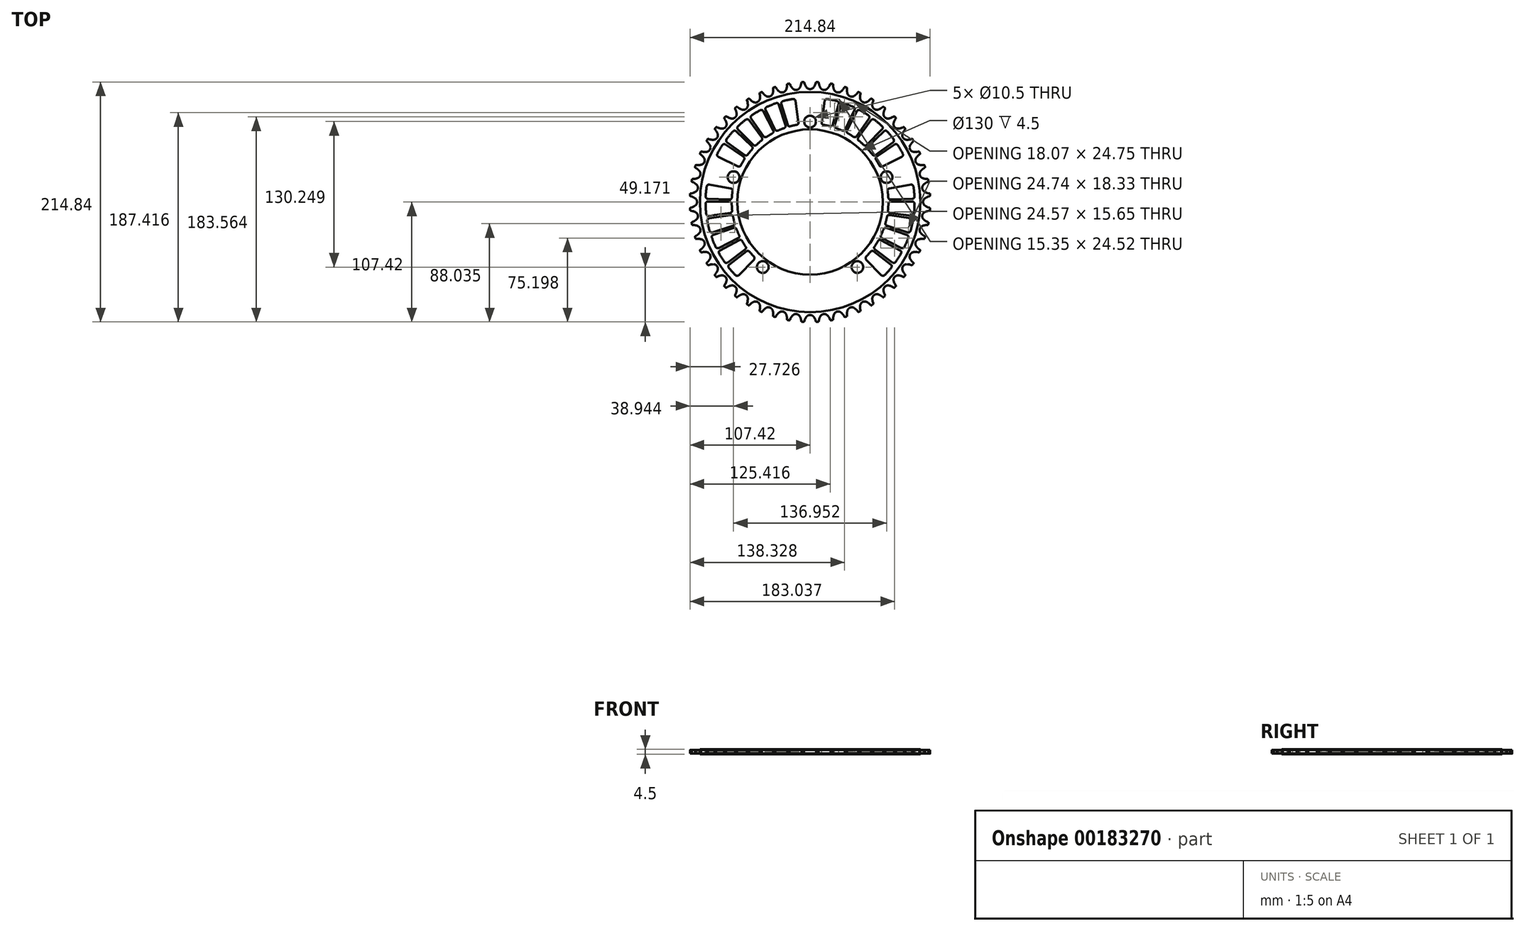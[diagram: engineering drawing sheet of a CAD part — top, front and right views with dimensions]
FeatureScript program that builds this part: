
annotation { "Feature Type Name" : "Feature", "Feature Type Description" : "" }
export const myFeature = defineFeature(function(context is Context, id is Id, definition is map)
    precondition{}
    {
        {
            var Q0;
            Q0=qCreatedBy(makeId("Top.planeOp"),FACE);
            var sketch = newSketch(context, id + "F0", { "sketchPlane" : qUnion([Q0])});
            skArc(sketch, "E0", {"start": v(-3.24, 102.74) * mm, "mid": v(-1.82, 101.53) * mm, "end": v(0, 101.1) * mm});
            skArc(sketch, "E1", {"start": v(-4.68, 105.43) * mm, "mid": v(-4.06, 104.03) * mm, "end": v(-3.24, 102.74) * mm});
            skLineSegment(sketch, "E2", {"start": v(-4.68, 105.43) * mm, "end": v(-5.06, 106.54) * mm});
            skArc(sketch, "E3.trimOffspring", {"start": v(-5.06, 106.54) * mm, "mid": v(-5.7, 107.84) * mm, "end": v(-6.6, 108.97) * mm});
            skArc(sketch, "E4.MirrorCS", {"start": v(3.24, 102.74) * mm, "mid": v(1.82, 101.53) * mm, "end": v(0, 101.1) * mm});
            skArc(sketch, "E5.MirrorCS", {"start": v(4.68, 105.43) * mm, "mid": v(4.06, 104.03) * mm, "end": v(3.24, 102.74) * mm});
            skLineSegment(sketch, "E6.MirrorCS", {"start": v(4.68, 105.43) * mm, "end": v(5.06, 106.54) * mm});
            skArc(sketch, "E7.MirrorCS", {"start": v(5.06, 106.54) * mm, "mid": v(5.7, 107.84) * mm, "end": v(6.6, 108.97) * mm});
            skArc(sketch, "E8.1.0", {"start": v(-17.35, 104.1) * mm, "mid": v(-16.57, 102.79) * mm, "end": v(-15.6, 101.6) * mm});
            skArc(sketch, "E8.1.1", {"start": v(-17.87, 105.16) * mm, "mid": v(-18.65, 106.37) * mm, "end": v(-19.68, 107.38) * mm});
            skArc(sketch, "E8.1.2", {"start": v(-9.17, 102.38) * mm, "mid": v(-10.43, 101) * mm, "end": v(-12.19, 100.35) * mm});
            skArc(sketch, "E8.1.3", {"start": v(-7.81, 106.38) * mm, "mid": v(-7.35, 107.74) * mm, "end": v(-6.6, 108.97) * mm});
            skArc(sketch, "E8.1.4", {"start": v(-15.6, 101.6) * mm, "mid": v(-14.04, 100.57) * mm, "end": v(-12.19, 100.35) * mm});
            skArc(sketch, "E8.1.5", {"start": v(-8.07, 105.23) * mm, "mid": v(-8.5, 103.76) * mm, "end": v(-9.17, 102.38) * mm});
            skLineSegment(sketch, "E8.1.6", {"start": v(-17.35, 104.1) * mm, "end": v(-17.87, 105.16) * mm});
            skLineSegment(sketch, "E8.1.7", {"start": v(-8.07, 105.23) * mm, "end": v(-7.81, 106.38) * mm});
            skArc(sketch, "E8.2.0", {"start": v(-29.77, 101.25) * mm, "mid": v(-28.84, 100.04) * mm, "end": v(-27.73, 98.98) * mm});
            skArc(sketch, "E8.2.1", {"start": v(-30.41, 102.23) * mm, "mid": v(-31.33, 103.35) * mm, "end": v(-32.48, 104.23) * mm});
            skArc(sketch, "E8.2.2", {"start": v(-21.44, 100.53) * mm, "mid": v(-22.53, 99.01) * mm, "end": v(-24.2, 98.15) * mm});
            skArc(sketch, "E8.2.3", {"start": v(-20.58, 104.66) * mm, "mid": v(-20.28, 106.07) * mm, "end": v(-19.68, 107.38) * mm});
            skArc(sketch, "E8.2.4", {"start": v(-27.73, 98.98) * mm, "mid": v(-26.06, 98.14) * mm, "end": v(-24.2, 98.15) * mm});
            skArc(sketch, "E8.2.5", {"start": v(-20.7, 103.5) * mm, "mid": v(-20.96, 101.98) * mm, "end": v(-21.44, 100.53) * mm});
            skLineSegment(sketch, "E8.2.6", {"start": v(-29.77, 101.25) * mm, "end": v(-30.41, 102.23) * mm});
            skLineSegment(sketch, "E8.2.7", {"start": v(-20.7, 103.5) * mm, "end": v(-20.58, 104.66) * mm});
            skArc(sketch, "E8.3.0", {"start": v(-41.76, 96.92) * mm, "mid": v(-40.69, 95.83) * mm, "end": v(-39.46, 94.91) * mm});
            skArc(sketch, "E8.3.1", {"start": v(-42.52, 97.82) * mm, "mid": v(-43.56, 98.82) * mm, "end": v(-44.8, 99.55) * mm});
            skArc(sketch, "E8.3.2", {"start": v(-33.4, 97.21) * mm, "mid": v(-34.3, 95.57) * mm, "end": v(-35.85, 94.52) * mm});
            skArc(sketch, "E8.3.3", {"start": v(-33.05, 101.42) * mm, "mid": v(-32.92, 102.85) * mm, "end": v(-32.48, 104.23) * mm});
            skArc(sketch, "E8.3.4", {"start": v(-39.46, 94.91) * mm, "mid": v(-37.7, 94.28) * mm, "end": v(-35.85, 94.52) * mm});
            skArc(sketch, "E8.3.5", {"start": v(-33.01, 100.24) * mm, "mid": v(-33.1, 98.71) * mm, "end": v(-33.4, 97.21) * mm});
            skLineSegment(sketch, "E8.3.6", {"start": v(-41.76, 96.92) * mm, "end": v(-42.52, 97.82) * mm});
            skLineSegment(sketch, "E8.3.7", {"start": v(-33.01, 100.24) * mm, "end": v(-33.05, 101.42) * mm});
            skArc(sketch, "E8.4.0", {"start": v(-53.14, 91.18) * mm, "mid": v(-51.94, 90.23) * mm, "end": v(-50.61, 89.46) * mm});
            skArc(sketch, "E8.4.1", {"start": v(-54, 91.99) * mm, "mid": v(-55.16, 92.85) * mm, "end": v(-56.48, 93.43) * mm});
            skArc(sketch, "E8.4.2", {"start": v(-44.87, 92.48) * mm, "mid": v(-45.57, 90.74) * mm, "end": v(-46.98, 89.51) * mm});
            skArc(sketch, "E8.4.3", {"start": v(-45.03, 96.7) * mm, "mid": v(-45.08, 98.13) * mm, "end": v(-44.8, 99.55) * mm});
            skArc(sketch, "E8.4.4", {"start": v(-50.61, 89.46) * mm, "mid": v(-48.8, 89.05) * mm, "end": v(-46.98, 89.51) * mm});
            skArc(sketch, "E8.4.5", {"start": v(-44.86, 95.53) * mm, "mid": v(-44.75, 94) * mm, "end": v(-44.87, 92.48) * mm});
            skLineSegment(sketch, "E8.4.6", {"start": v(-53.14, 91.18) * mm, "end": v(-54, 91.99) * mm});
            skLineSegment(sketch, "E8.4.7", {"start": v(-44.86, 95.53) * mm, "end": v(-45.03, 96.7) * mm});
            skArc(sketch, "E8.5.0", {"start": v(-63.74, 84.11) * mm, "mid": v(-62.44, 83.31) * mm, "end": v(-61.03, 82.7) * mm});
            skArc(sketch, "E8.5.1", {"start": v(-64.7, 84.8) * mm, "mid": v(-65.94, 85.52) * mm, "end": v(-67.33, 85.94) * mm});
            skArc(sketch, "E8.5.2", {"start": v(-55.7, 86.4) * mm, "mid": v(-56.18, 84.59) * mm, "end": v(-57.43, 83.2) * mm});
            skArc(sketch, "E8.5.3", {"start": v(-56.36, 90.56) * mm, "mid": v(-56.58, 91.99) * mm, "end": v(-56.48, 93.43) * mm});
            skArc(sketch, "E8.5.4", {"start": v(-61.03, 82.7) * mm, "mid": v(-59.17, 82.52) * mm, "end": v(-57.43, 83.2) * mm});
            skArc(sketch, "E8.5.5", {"start": v(-56.04, 89.43) * mm, "mid": v(-55.76, 87.92) * mm, "end": v(-55.7, 86.4) * mm});
            skLineSegment(sketch, "E8.5.6", {"start": v(-63.74, 84.11) * mm, "end": v(-64.7, 84.8) * mm});
            skLineSegment(sketch, "E8.5.7", {"start": v(-56.04, 89.43) * mm, "end": v(-56.36, 90.56) * mm});
            skArc(sketch, "E8.6.0", {"start": v(-73.42, 75.82) * mm, "mid": v(-72.03, 75.18) * mm, "end": v(-70.55, 74.75) * mm});
            skArc(sketch, "E8.6.1", {"start": v(-74.44, 76.4) * mm, "mid": v(-75.77, 76.95) * mm, "end": v(-77.2, 77.2) * mm});
            skArc(sketch, "E8.6.2", {"start": v(-65.7, 79.05) * mm, "mid": v(-65.96, 77.2) * mm, "end": v(-67.04, 75.67) * mm});
            skArc(sketch, "E8.6.3", {"start": v(-66.86, 83.1) * mm, "mid": v(-67.25, 84.5) * mm, "end": v(-67.33, 85.94) * mm});
            skArc(sketch, "E8.6.4", {"start": v(-70.55, 74.75) * mm, "mid": v(-68.68, 74.79) * mm, "end": v(-67.04, 75.67) * mm});
            skArc(sketch, "E8.6.5", {"start": v(-66.41, 82.02) * mm, "mid": v(-65.95, 80.56) * mm, "end": v(-65.7, 79.05) * mm});
            skLineSegment(sketch, "E8.6.6", {"start": v(-73.42, 75.82) * mm, "end": v(-74.44, 76.4) * mm});
            skLineSegment(sketch, "E8.6.7", {"start": v(-66.41, 82.02) * mm, "end": v(-66.86, 83.1) * mm});
            skArc(sketch, "E8.7.0", {"start": v(-82.02, 66.41) * mm, "mid": v(-80.56, 65.95) * mm, "end": v(-79.05, 65.7) * mm});
            skArc(sketch, "E8.7.1", {"start": v(-83.1, 66.86) * mm, "mid": v(-84.5, 67.25) * mm, "end": v(-85.94, 67.33) * mm});
            skArc(sketch, "E8.7.2", {"start": v(-74.75, 70.55) * mm, "mid": v(-74.79, 68.68) * mm, "end": v(-75.67, 67.04) * mm});
            skArc(sketch, "E8.7.3", {"start": v(-76.4, 74.44) * mm, "mid": v(-76.95, 75.77) * mm, "end": v(-77.2, 77.2) * mm});
            skArc(sketch, "E8.7.4", {"start": v(-79.05, 65.7) * mm, "mid": v(-77.2, 65.96) * mm, "end": v(-75.67, 67.04) * mm});
            skArc(sketch, "E8.7.5", {"start": v(-75.82, 73.42) * mm, "mid": v(-75.18, 72.03) * mm, "end": v(-74.75, 70.55) * mm});
            skLineSegment(sketch, "E8.7.6", {"start": v(-82.02, 66.41) * mm, "end": v(-83.1, 66.86) * mm});
            skLineSegment(sketch, "E8.7.7", {"start": v(-75.82, 73.42) * mm, "end": v(-76.4, 74.44) * mm});
            skArc(sketch, "E8.8.0", {"start": v(-89.43, 56.04) * mm, "mid": v(-87.92, 55.76) * mm, "end": v(-86.4, 55.7) * mm});
            skArc(sketch, "E8.8.1", {"start": v(-90.56, 56.36) * mm, "mid": v(-91.99, 56.58) * mm, "end": v(-93.43, 56.48) * mm});
            skArc(sketch, "E8.8.2", {"start": v(-82.7, 61.03) * mm, "mid": v(-82.52, 59.17) * mm, "end": v(-83.2, 57.43) * mm});
            skArc(sketch, "E8.8.3", {"start": v(-84.8, 64.7) * mm, "mid": v(-85.52, 65.94) * mm, "end": v(-85.94, 67.33) * mm});
            skArc(sketch, "E8.8.4", {"start": v(-86.4, 55.7) * mm, "mid": v(-84.59, 56.18) * mm, "end": v(-83.2, 57.43) * mm});
            skArc(sketch, "E8.8.5", {"start": v(-84.11, 63.74) * mm, "mid": v(-83.31, 62.44) * mm, "end": v(-82.7, 61.03) * mm});
            skLineSegment(sketch, "E8.8.6", {"start": v(-89.43, 56.04) * mm, "end": v(-90.56, 56.36) * mm});
            skLineSegment(sketch, "E8.8.7", {"start": v(-84.11, 63.74) * mm, "end": v(-84.8, 64.7) * mm});
            skArc(sketch, "E8.9.0", {"start": v(-95.53, 44.86) * mm, "mid": v(-94, 44.75) * mm, "end": v(-92.48, 44.87) * mm});
            skArc(sketch, "E8.9.1", {"start": v(-96.7, 45.03) * mm, "mid": v(-98.13, 45.08) * mm, "end": v(-99.55, 44.8) * mm});
            skArc(sketch, "E8.9.2", {"start": v(-89.46, 50.61) * mm, "mid": v(-89.05, 48.8) * mm, "end": v(-89.51, 46.98) * mm});
            skArc(sketch, "E8.9.3", {"start": v(-91.99, 54) * mm, "mid": v(-92.85, 55.16) * mm, "end": v(-93.43, 56.48) * mm});
            skArc(sketch, "E8.9.4", {"start": v(-92.48, 44.87) * mm, "mid": v(-90.74, 45.57) * mm, "end": v(-89.51, 46.98) * mm});
            skArc(sketch, "E8.9.5", {"start": v(-91.18, 53.14) * mm, "mid": v(-90.23, 51.94) * mm, "end": v(-89.46, 50.61) * mm});
            skLineSegment(sketch, "E8.9.6", {"start": v(-95.53, 44.86) * mm, "end": v(-96.7, 45.03) * mm});
            skLineSegment(sketch, "E8.9.7", {"start": v(-91.18, 53.14) * mm, "end": v(-91.99, 54) * mm});
            skArc(sketch, "E8.10.0", {"start": v(-100.24, 33.01) * mm, "mid": v(-98.71, 33.1) * mm, "end": v(-97.21, 33.4) * mm});
            skArc(sketch, "E8.10.1", {"start": v(-101.42, 33.05) * mm, "mid": v(-102.85, 32.92) * mm, "end": v(-104.23, 32.48) * mm});
            skArc(sketch, "E8.10.2", {"start": v(-94.91, 39.46) * mm, "mid": v(-94.28, 37.7) * mm, "end": v(-94.52, 35.85) * mm});
            skArc(sketch, "E8.10.3", {"start": v(-97.82, 42.52) * mm, "mid": v(-98.82, 43.56) * mm, "end": v(-99.55, 44.8) * mm});
            skArc(sketch, "E8.10.4", {"start": v(-97.21, 33.4) * mm, "mid": v(-95.57, 34.3) * mm, "end": v(-94.52, 35.85) * mm});
            skArc(sketch, "E8.10.5", {"start": v(-96.92, 41.76) * mm, "mid": v(-95.83, 40.69) * mm, "end": v(-94.91, 39.46) * mm});
            skLineSegment(sketch, "E8.10.6", {"start": v(-100.24, 33.01) * mm, "end": v(-101.42, 33.05) * mm});
            skLineSegment(sketch, "E8.10.7", {"start": v(-96.92, 41.76) * mm, "end": v(-97.82, 42.52) * mm});
            skArc(sketch, "E8.11.0", {"start": v(-103.5, 20.7) * mm, "mid": v(-101.98, 20.96) * mm, "end": v(-100.53, 21.44) * mm});
            skArc(sketch, "E8.11.1", {"start": v(-104.66, 20.58) * mm, "mid": v(-106.07, 20.28) * mm, "end": v(-107.38, 19.68) * mm});
            skArc(sketch, "E8.11.2", {"start": v(-98.98, 27.73) * mm, "mid": v(-98.14, 26.06) * mm, "end": v(-98.15, 24.2) * mm});
            skArc(sketch, "E8.11.3", {"start": v(-102.23, 30.41) * mm, "mid": v(-103.35, 31.33) * mm, "end": v(-104.23, 32.48) * mm});
            skArc(sketch, "E8.11.4", {"start": v(-100.53, 21.44) * mm, "mid": v(-99.01, 22.53) * mm, "end": v(-98.15, 24.2) * mm});
            skArc(sketch, "E8.11.5", {"start": v(-101.25, 29.77) * mm, "mid": v(-100.04, 28.84) * mm, "end": v(-98.98, 27.73) * mm});
            skLineSegment(sketch, "E8.11.6", {"start": v(-103.5, 20.7) * mm, "end": v(-104.66, 20.58) * mm});
            skLineSegment(sketch, "E8.11.7", {"start": v(-101.25, 29.77) * mm, "end": v(-102.23, 30.41) * mm});
            skArc(sketch, "E8.12.0", {"start": v(-105.23, 8.07) * mm, "mid": v(-103.76, 8.5) * mm, "end": v(-102.38, 9.17) * mm});
            skArc(sketch, "E8.12.1", {"start": v(-106.38, 7.81) * mm, "mid": v(-107.74, 7.35) * mm, "end": v(-108.97, 6.6) * mm});
            skArc(sketch, "E8.12.2", {"start": v(-101.6, 15.6) * mm, "mid": v(-100.57, 14.04) * mm, "end": v(-100.35, 12.19) * mm});
            skArc(sketch, "E8.12.3", {"start": v(-105.16, 17.87) * mm, "mid": v(-106.37, 18.65) * mm, "end": v(-107.38, 19.68) * mm});
            skArc(sketch, "E8.12.4", {"start": v(-102.38, 9.17) * mm, "mid": v(-101, 10.43) * mm, "end": v(-100.35, 12.19) * mm});
            skArc(sketch, "E8.12.5", {"start": v(-104.1, 17.35) * mm, "mid": v(-102.79, 16.57) * mm, "end": v(-101.6, 15.6) * mm});
            skLineSegment(sketch, "E8.12.6", {"start": v(-105.23, 8.07) * mm, "end": v(-106.38, 7.81) * mm});
            skLineSegment(sketch, "E8.12.7", {"start": v(-104.1, 17.35) * mm, "end": v(-105.16, 17.87) * mm});
            skArc(sketch, "E8.13.0", {"start": v(-105.43, -4.68) * mm, "mid": v(-104.03, -4.06) * mm, "end": v(-102.74, -3.24) * mm});
            skArc(sketch, "E8.13.1", {"start": v(-106.54, -5.06) * mm, "mid": v(-107.84, -5.7) * mm, "end": v(-108.97, -6.6) * mm});
            skArc(sketch, "E8.13.2", {"start": v(-102.74, 3.24) * mm, "mid": v(-101.53, 1.82) * mm, "end": v(-101.1, 0) * mm});
            skArc(sketch, "E8.13.3", {"start": v(-106.54, 5.06) * mm, "mid": v(-107.84, 5.7) * mm, "end": v(-108.97, 6.6) * mm});
            skArc(sketch, "E8.13.4", {"start": v(-102.74, -3.24) * mm, "mid": v(-101.53, -1.82) * mm, "end": v(-101.1, 0) * mm});
            skArc(sketch, "E8.13.5", {"start": v(-105.43, 4.68) * mm, "mid": v(-104.03, 4.06) * mm, "end": v(-102.74, 3.24) * mm});
            skLineSegment(sketch, "E8.13.6", {"start": v(-105.43, -4.68) * mm, "end": v(-106.54, -5.06) * mm});
            skLineSegment(sketch, "E8.13.7", {"start": v(-105.43, 4.68) * mm, "end": v(-106.54, 5.06) * mm});
            skArc(sketch, "E8.14.0", {"start": v(-104.1, -17.35) * mm, "mid": v(-102.79, -16.57) * mm, "end": v(-101.6, -15.6) * mm});
            skArc(sketch, "E8.14.1", {"start": v(-105.16, -17.87) * mm, "mid": v(-106.37, -18.65) * mm, "end": v(-107.38, -19.68) * mm});
            skArc(sketch, "E8.14.2", {"start": v(-102.38, -9.17) * mm, "mid": v(-101, -10.43) * mm, "end": v(-100.35, -12.19) * mm});
            skArc(sketch, "E8.14.3", {"start": v(-106.38, -7.81) * mm, "mid": v(-107.74, -7.35) * mm, "end": v(-108.97, -6.6) * mm});
            skArc(sketch, "E8.14.4", {"start": v(-101.6, -15.6) * mm, "mid": v(-100.57, -14.04) * mm, "end": v(-100.35, -12.19) * mm});
            skArc(sketch, "E8.14.5", {"start": v(-105.23, -8.07) * mm, "mid": v(-103.76, -8.5) * mm, "end": v(-102.38, -9.17) * mm});
            skLineSegment(sketch, "E8.14.6", {"start": v(-104.1, -17.35) * mm, "end": v(-105.16, -17.87) * mm});
            skLineSegment(sketch, "E8.14.7", {"start": v(-105.23, -8.07) * mm, "end": v(-106.38, -7.81) * mm});
            skArc(sketch, "E8.15.0", {"start": v(-101.25, -29.77) * mm, "mid": v(-100.04, -28.84) * mm, "end": v(-98.98, -27.73) * mm});
            skArc(sketch, "E8.15.1", {"start": v(-102.23, -30.41) * mm, "mid": v(-103.35, -31.33) * mm, "end": v(-104.23, -32.48) * mm});
            skArc(sketch, "E8.15.2", {"start": v(-100.53, -21.44) * mm, "mid": v(-99.01, -22.53) * mm, "end": v(-98.15, -24.2) * mm});
            skArc(sketch, "E8.15.3", {"start": v(-104.66, -20.58) * mm, "mid": v(-106.07, -20.28) * mm, "end": v(-107.38, -19.68) * mm});
            skArc(sketch, "E8.15.4", {"start": v(-98.98, -27.73) * mm, "mid": v(-98.14, -26.06) * mm, "end": v(-98.15, -24.2) * mm});
            skArc(sketch, "E8.15.5", {"start": v(-103.5, -20.7) * mm, "mid": v(-101.98, -20.96) * mm, "end": v(-100.53, -21.44) * mm});
            skLineSegment(sketch, "E8.15.6", {"start": v(-101.25, -29.77) * mm, "end": v(-102.23, -30.41) * mm});
            skLineSegment(sketch, "E8.15.7", {"start": v(-103.5, -20.7) * mm, "end": v(-104.66, -20.58) * mm});
            skArc(sketch, "E8.16.0", {"start": v(-96.92, -41.76) * mm, "mid": v(-95.83, -40.69) * mm, "end": v(-94.91, -39.46) * mm});
            skArc(sketch, "E8.16.1", {"start": v(-97.82, -42.52) * mm, "mid": v(-98.82, -43.56) * mm, "end": v(-99.55, -44.8) * mm});
            skArc(sketch, "E8.16.2", {"start": v(-97.21, -33.4) * mm, "mid": v(-95.57, -34.3) * mm, "end": v(-94.52, -35.85) * mm});
            skArc(sketch, "E8.16.3", {"start": v(-101.42, -33.05) * mm, "mid": v(-102.85, -32.92) * mm, "end": v(-104.23, -32.48) * mm});
            skArc(sketch, "E8.16.4", {"start": v(-94.91, -39.46) * mm, "mid": v(-94.28, -37.7) * mm, "end": v(-94.52, -35.85) * mm});
            skArc(sketch, "E8.16.5", {"start": v(-100.24, -33.01) * mm, "mid": v(-98.71, -33.1) * mm, "end": v(-97.21, -33.4) * mm});
            skLineSegment(sketch, "E8.16.6", {"start": v(-96.92, -41.76) * mm, "end": v(-97.82, -42.52) * mm});
            skLineSegment(sketch, "E8.16.7", {"start": v(-100.24, -33.01) * mm, "end": v(-101.42, -33.05) * mm});
            skArc(sketch, "E8.17.0", {"start": v(-91.18, -53.14) * mm, "mid": v(-90.23, -51.94) * mm, "end": v(-89.46, -50.61) * mm});
            skArc(sketch, "E8.17.1", {"start": v(-91.99, -54) * mm, "mid": v(-92.85, -55.16) * mm, "end": v(-93.43, -56.48) * mm});
            skArc(sketch, "E8.17.2", {"start": v(-92.48, -44.87) * mm, "mid": v(-90.74, -45.57) * mm, "end": v(-89.51, -46.98) * mm});
            skArc(sketch, "E8.17.3", {"start": v(-96.7, -45.03) * mm, "mid": v(-98.13, -45.08) * mm, "end": v(-99.55, -44.8) * mm});
            skArc(sketch, "E8.17.4", {"start": v(-89.46, -50.61) * mm, "mid": v(-89.05, -48.8) * mm, "end": v(-89.51, -46.98) * mm});
            skArc(sketch, "E8.17.5", {"start": v(-95.53, -44.86) * mm, "mid": v(-94, -44.75) * mm, "end": v(-92.48, -44.87) * mm});
            skLineSegment(sketch, "E8.17.6", {"start": v(-91.18, -53.14) * mm, "end": v(-91.99, -54) * mm});
            skLineSegment(sketch, "E8.17.7", {"start": v(-95.53, -44.86) * mm, "end": v(-96.7, -45.03) * mm});
            skArc(sketch, "E8.18.0", {"start": v(-84.11, -63.74) * mm, "mid": v(-83.31, -62.44) * mm, "end": v(-82.7, -61.03) * mm});
            skArc(sketch, "E8.18.1", {"start": v(-84.8, -64.7) * mm, "mid": v(-85.52, -65.94) * mm, "end": v(-85.94, -67.33) * mm});
            skArc(sketch, "E8.18.2", {"start": v(-86.4, -55.7) * mm, "mid": v(-84.59, -56.18) * mm, "end": v(-83.2, -57.43) * mm});
            skArc(sketch, "E8.18.3", {"start": v(-90.56, -56.36) * mm, "mid": v(-91.99, -56.58) * mm, "end": v(-93.43, -56.48) * mm});
            skArc(sketch, "E8.18.4", {"start": v(-82.7, -61.03) * mm, "mid": v(-82.52, -59.17) * mm, "end": v(-83.2, -57.43) * mm});
            skArc(sketch, "E8.18.5", {"start": v(-89.43, -56.04) * mm, "mid": v(-87.92, -55.76) * mm, "end": v(-86.4, -55.7) * mm});
            skLineSegment(sketch, "E8.18.6", {"start": v(-84.11, -63.74) * mm, "end": v(-84.8, -64.7) * mm});
            skLineSegment(sketch, "E8.18.7", {"start": v(-89.43, -56.04) * mm, "end": v(-90.56, -56.36) * mm});
            skArc(sketch, "E8.19.0", {"start": v(-75.82, -73.42) * mm, "mid": v(-75.18, -72.03) * mm, "end": v(-74.75, -70.55) * mm});
            skArc(sketch, "E8.19.1", {"start": v(-76.4, -74.44) * mm, "mid": v(-76.95, -75.77) * mm, "end": v(-77.2, -77.2) * mm});
            skArc(sketch, "E8.19.2", {"start": v(-79.05, -65.7) * mm, "mid": v(-77.2, -65.96) * mm, "end": v(-75.67, -67.04) * mm});
            skArc(sketch, "E8.19.3", {"start": v(-83.1, -66.86) * mm, "mid": v(-84.5, -67.25) * mm, "end": v(-85.94, -67.33) * mm});
            skArc(sketch, "E8.19.4", {"start": v(-74.75, -70.55) * mm, "mid": v(-74.79, -68.68) * mm, "end": v(-75.67, -67.04) * mm});
            skArc(sketch, "E8.19.5", {"start": v(-82.02, -66.41) * mm, "mid": v(-80.56, -65.95) * mm, "end": v(-79.05, -65.7) * mm});
            skLineSegment(sketch, "E8.19.6", {"start": v(-75.82, -73.42) * mm, "end": v(-76.4, -74.44) * mm});
            skLineSegment(sketch, "E8.19.7", {"start": v(-82.02, -66.41) * mm, "end": v(-83.1, -66.86) * mm});
            skArc(sketch, "E8.20.0", {"start": v(-66.41, -82.02) * mm, "mid": v(-65.95, -80.56) * mm, "end": v(-65.7, -79.05) * mm});
            skArc(sketch, "E8.20.1", {"start": v(-66.86, -83.1) * mm, "mid": v(-67.25, -84.5) * mm, "end": v(-67.33, -85.94) * mm});
            skArc(sketch, "E8.20.2", {"start": v(-70.55, -74.75) * mm, "mid": v(-68.68, -74.79) * mm, "end": v(-67.04, -75.67) * mm});
            skArc(sketch, "E8.20.3", {"start": v(-74.44, -76.4) * mm, "mid": v(-75.77, -76.95) * mm, "end": v(-77.2, -77.2) * mm});
            skArc(sketch, "E8.20.4", {"start": v(-65.7, -79.05) * mm, "mid": v(-65.96, -77.2) * mm, "end": v(-67.04, -75.67) * mm});
            skArc(sketch, "E8.20.5", {"start": v(-73.42, -75.82) * mm, "mid": v(-72.03, -75.18) * mm, "end": v(-70.55, -74.75) * mm});
            skLineSegment(sketch, "E8.20.6", {"start": v(-66.41, -82.02) * mm, "end": v(-66.86, -83.1) * mm});
            skLineSegment(sketch, "E8.20.7", {"start": v(-73.42, -75.82) * mm, "end": v(-74.44, -76.4) * mm});
            skArc(sketch, "E8.21.0", {"start": v(-56.04, -89.43) * mm, "mid": v(-55.76, -87.92) * mm, "end": v(-55.7, -86.4) * mm});
            skArc(sketch, "E8.21.1", {"start": v(-56.36, -90.56) * mm, "mid": v(-56.58, -91.99) * mm, "end": v(-56.48, -93.43) * mm});
            skArc(sketch, "E8.21.2", {"start": v(-61.03, -82.7) * mm, "mid": v(-59.17, -82.52) * mm, "end": v(-57.43, -83.2) * mm});
            skArc(sketch, "E8.21.3", {"start": v(-64.7, -84.8) * mm, "mid": v(-65.94, -85.52) * mm, "end": v(-67.33, -85.94) * mm});
            skArc(sketch, "E8.21.4", {"start": v(-55.7, -86.4) * mm, "mid": v(-56.18, -84.59) * mm, "end": v(-57.43, -83.2) * mm});
            skArc(sketch, "E8.21.5", {"start": v(-63.74, -84.11) * mm, "mid": v(-62.44, -83.31) * mm, "end": v(-61.03, -82.7) * mm});
            skLineSegment(sketch, "E8.21.6", {"start": v(-56.04, -89.43) * mm, "end": v(-56.36, -90.56) * mm});
            skLineSegment(sketch, "E8.21.7", {"start": v(-63.74, -84.11) * mm, "end": v(-64.7, -84.8) * mm});
            skArc(sketch, "E8.22.0", {"start": v(-44.86, -95.53) * mm, "mid": v(-44.75, -94) * mm, "end": v(-44.87, -92.48) * mm});
            skArc(sketch, "E8.22.1", {"start": v(-45.03, -96.7) * mm, "mid": v(-45.08, -98.13) * mm, "end": v(-44.8, -99.55) * mm});
            skArc(sketch, "E8.22.2", {"start": v(-50.61, -89.46) * mm, "mid": v(-48.8, -89.05) * mm, "end": v(-46.98, -89.51) * mm});
            skArc(sketch, "E8.22.3", {"start": v(-54, -91.99) * mm, "mid": v(-55.16, -92.85) * mm, "end": v(-56.48, -93.43) * mm});
            skArc(sketch, "E8.22.4", {"start": v(-44.87, -92.48) * mm, "mid": v(-45.57, -90.74) * mm, "end": v(-46.98, -89.51) * mm});
            skArc(sketch, "E8.22.5", {"start": v(-53.14, -91.18) * mm, "mid": v(-51.94, -90.23) * mm, "end": v(-50.61, -89.46) * mm});
            skLineSegment(sketch, "E8.22.6", {"start": v(-44.86, -95.53) * mm, "end": v(-45.03, -96.7) * mm});
            skLineSegment(sketch, "E8.22.7", {"start": v(-53.14, -91.18) * mm, "end": v(-54, -91.99) * mm});
            skArc(sketch, "E8.23.0", {"start": v(-33.01, -100.24) * mm, "mid": v(-33.1, -98.71) * mm, "end": v(-33.4, -97.21) * mm});
            skArc(sketch, "E8.23.1", {"start": v(-33.05, -101.42) * mm, "mid": v(-32.92, -102.85) * mm, "end": v(-32.48, -104.23) * mm});
            skArc(sketch, "E8.23.2", {"start": v(-39.46, -94.91) * mm, "mid": v(-37.7, -94.28) * mm, "end": v(-35.85, -94.52) * mm});
            skArc(sketch, "E8.23.3", {"start": v(-42.52, -97.82) * mm, "mid": v(-43.56, -98.82) * mm, "end": v(-44.8, -99.55) * mm});
            skArc(sketch, "E8.23.4", {"start": v(-33.4, -97.21) * mm, "mid": v(-34.3, -95.57) * mm, "end": v(-35.85, -94.52) * mm});
            skArc(sketch, "E8.23.5", {"start": v(-41.76, -96.92) * mm, "mid": v(-40.69, -95.83) * mm, "end": v(-39.46, -94.91) * mm});
            skLineSegment(sketch, "E8.23.6", {"start": v(-33.01, -100.24) * mm, "end": v(-33.05, -101.42) * mm});
            skLineSegment(sketch, "E8.23.7", {"start": v(-41.76, -96.92) * mm, "end": v(-42.52, -97.82) * mm});
            skArc(sketch, "E8.24.0", {"start": v(-20.7, -103.5) * mm, "mid": v(-20.96, -101.98) * mm, "end": v(-21.44, -100.53) * mm});
            skArc(sketch, "E8.24.1", {"start": v(-20.58, -104.66) * mm, "mid": v(-20.28, -106.07) * mm, "end": v(-19.68, -107.38) * mm});
            skArc(sketch, "E8.24.2", {"start": v(-27.73, -98.98) * mm, "mid": v(-26.06, -98.14) * mm, "end": v(-24.2, -98.15) * mm});
            skArc(sketch, "E8.24.3", {"start": v(-30.41, -102.23) * mm, "mid": v(-31.33, -103.35) * mm, "end": v(-32.48, -104.23) * mm});
            skArc(sketch, "E8.24.4", {"start": v(-21.44, -100.53) * mm, "mid": v(-22.53, -99.01) * mm, "end": v(-24.2, -98.15) * mm});
            skArc(sketch, "E8.24.5", {"start": v(-29.77, -101.25) * mm, "mid": v(-28.84, -100.04) * mm, "end": v(-27.73, -98.98) * mm});
            skLineSegment(sketch, "E8.24.6", {"start": v(-20.7, -103.5) * mm, "end": v(-20.58, -104.66) * mm});
            skLineSegment(sketch, "E8.24.7", {"start": v(-29.77, -101.25) * mm, "end": v(-30.41, -102.23) * mm});
            skArc(sketch, "E8.25.0", {"start": v(-8.07, -105.23) * mm, "mid": v(-8.5, -103.76) * mm, "end": v(-9.17, -102.38) * mm});
            skArc(sketch, "E8.25.1", {"start": v(-7.81, -106.38) * mm, "mid": v(-7.35, -107.74) * mm, "end": v(-6.6, -108.97) * mm});
            skArc(sketch, "E8.25.2", {"start": v(-15.6, -101.6) * mm, "mid": v(-14.04, -100.57) * mm, "end": v(-12.19, -100.35) * mm});
            skArc(sketch, "E8.25.3", {"start": v(-17.87, -105.16) * mm, "mid": v(-18.65, -106.37) * mm, "end": v(-19.68, -107.38) * mm});
            skArc(sketch, "E8.25.4", {"start": v(-9.17, -102.38) * mm, "mid": v(-10.43, -101) * mm, "end": v(-12.19, -100.35) * mm});
            skArc(sketch, "E8.25.5", {"start": v(-17.35, -104.1) * mm, "mid": v(-16.57, -102.79) * mm, "end": v(-15.6, -101.6) * mm});
            skLineSegment(sketch, "E8.25.6", {"start": v(-8.07, -105.23) * mm, "end": v(-7.81, -106.38) * mm});
            skLineSegment(sketch, "E8.25.7", {"start": v(-17.35, -104.1) * mm, "end": v(-17.87, -105.16) * mm});
            skArc(sketch, "E8.26.0", {"start": v(4.68, -105.43) * mm, "mid": v(4.06, -104.03) * mm, "end": v(3.24, -102.74) * mm});
            skArc(sketch, "E8.26.1", {"start": v(5.06, -106.54) * mm, "mid": v(5.7, -107.84) * mm, "end": v(6.6, -108.97) * mm});
            skArc(sketch, "E8.26.2", {"start": v(-3.24, -102.74) * mm, "mid": v(-1.82, -101.53) * mm, "end": v(0, -101.1) * mm});
            skArc(sketch, "E8.26.3", {"start": v(-5.06, -106.54) * mm, "mid": v(-5.7, -107.84) * mm, "end": v(-6.6, -108.97) * mm});
            skArc(sketch, "E8.26.4", {"start": v(3.24, -102.74) * mm, "mid": v(1.82, -101.53) * mm, "end": v(0, -101.1) * mm});
            skArc(sketch, "E8.26.5", {"start": v(-4.68, -105.43) * mm, "mid": v(-4.06, -104.03) * mm, "end": v(-3.24, -102.74) * mm});
            skLineSegment(sketch, "E8.26.6", {"start": v(4.68, -105.43) * mm, "end": v(5.06, -106.54) * mm});
            skLineSegment(sketch, "E8.26.7", {"start": v(-4.68, -105.43) * mm, "end": v(-5.06, -106.54) * mm});
            skArc(sketch, "E8.27.0", {"start": v(17.35, -104.1) * mm, "mid": v(16.57, -102.79) * mm, "end": v(15.6, -101.6) * mm});
            skArc(sketch, "E8.27.1", {"start": v(17.87, -105.16) * mm, "mid": v(18.65, -106.37) * mm, "end": v(19.68, -107.38) * mm});
            skArc(sketch, "E8.27.2", {"start": v(9.17, -102.38) * mm, "mid": v(10.43, -101) * mm, "end": v(12.19, -100.35) * mm});
            skArc(sketch, "E8.27.3", {"start": v(7.81, -106.38) * mm, "mid": v(7.35, -107.74) * mm, "end": v(6.6, -108.97) * mm});
            skArc(sketch, "E8.27.4", {"start": v(15.6, -101.6) * mm, "mid": v(14.04, -100.57) * mm, "end": v(12.19, -100.35) * mm});
            skArc(sketch, "E8.27.5", {"start": v(8.07, -105.23) * mm, "mid": v(8.5, -103.76) * mm, "end": v(9.17, -102.38) * mm});
            skLineSegment(sketch, "E8.27.6", {"start": v(17.35, -104.1) * mm, "end": v(17.87, -105.16) * mm});
            skLineSegment(sketch, "E8.27.7", {"start": v(8.07, -105.23) * mm, "end": v(7.81, -106.38) * mm});
            skArc(sketch, "E8.28.0", {"start": v(29.77, -101.25) * mm, "mid": v(28.84, -100.04) * mm, "end": v(27.73, -98.98) * mm});
            skArc(sketch, "E8.28.1", {"start": v(30.41, -102.23) * mm, "mid": v(31.33, -103.35) * mm, "end": v(32.48, -104.23) * mm});
            skArc(sketch, "E8.28.2", {"start": v(21.44, -100.53) * mm, "mid": v(22.53, -99.01) * mm, "end": v(24.2, -98.15) * mm});
            skArc(sketch, "E8.28.3", {"start": v(20.58, -104.66) * mm, "mid": v(20.28, -106.07) * mm, "end": v(19.68, -107.38) * mm});
            skArc(sketch, "E8.28.4", {"start": v(27.73, -98.98) * mm, "mid": v(26.06, -98.14) * mm, "end": v(24.2, -98.15) * mm});
            skArc(sketch, "E8.28.5", {"start": v(20.7, -103.5) * mm, "mid": v(20.96, -101.98) * mm, "end": v(21.44, -100.53) * mm});
            skLineSegment(sketch, "E8.28.6", {"start": v(29.77, -101.25) * mm, "end": v(30.41, -102.23) * mm});
            skLineSegment(sketch, "E8.28.7", {"start": v(20.7, -103.5) * mm, "end": v(20.58, -104.66) * mm});
            skArc(sketch, "E8.29.0", {"start": v(41.76, -96.92) * mm, "mid": v(40.69, -95.83) * mm, "end": v(39.46, -94.91) * mm});
            skArc(sketch, "E8.29.1", {"start": v(42.52, -97.82) * mm, "mid": v(43.56, -98.82) * mm, "end": v(44.8, -99.55) * mm});
            skArc(sketch, "E8.29.2", {"start": v(33.4, -97.21) * mm, "mid": v(34.3, -95.57) * mm, "end": v(35.85, -94.52) * mm});
            skArc(sketch, "E8.29.3", {"start": v(33.05, -101.42) * mm, "mid": v(32.92, -102.85) * mm, "end": v(32.48, -104.23) * mm});
            skArc(sketch, "E8.29.4", {"start": v(39.46, -94.91) * mm, "mid": v(37.7, -94.28) * mm, "end": v(35.85, -94.52) * mm});
            skArc(sketch, "E8.29.5", {"start": v(33.01, -100.24) * mm, "mid": v(33.1, -98.71) * mm, "end": v(33.4, -97.21) * mm});
            skLineSegment(sketch, "E8.29.6", {"start": v(41.76, -96.92) * mm, "end": v(42.52, -97.82) * mm});
            skLineSegment(sketch, "E8.29.7", {"start": v(33.01, -100.24) * mm, "end": v(33.05, -101.42) * mm});
            skArc(sketch, "E8.30.0", {"start": v(53.14, -91.18) * mm, "mid": v(51.94, -90.23) * mm, "end": v(50.61, -89.46) * mm});
            skArc(sketch, "E8.30.1", {"start": v(54, -91.99) * mm, "mid": v(55.16, -92.85) * mm, "end": v(56.48, -93.43) * mm});
            skArc(sketch, "E8.30.2", {"start": v(44.87, -92.48) * mm, "mid": v(45.57, -90.74) * mm, "end": v(46.98, -89.51) * mm});
            skArc(sketch, "E8.30.3", {"start": v(45.03, -96.7) * mm, "mid": v(45.08, -98.13) * mm, "end": v(44.8, -99.55) * mm});
            skArc(sketch, "E8.30.4", {"start": v(50.61, -89.46) * mm, "mid": v(48.8, -89.05) * mm, "end": v(46.98, -89.51) * mm});
            skArc(sketch, "E8.30.5", {"start": v(44.86, -95.53) * mm, "mid": v(44.75, -94) * mm, "end": v(44.87, -92.48) * mm});
            skLineSegment(sketch, "E8.30.6", {"start": v(53.14, -91.18) * mm, "end": v(54, -91.99) * mm});
            skLineSegment(sketch, "E8.30.7", {"start": v(44.86, -95.53) * mm, "end": v(45.03, -96.7) * mm});
            skArc(sketch, "E8.31.0", {"start": v(63.74, -84.11) * mm, "mid": v(62.44, -83.31) * mm, "end": v(61.03, -82.7) * mm});
            skArc(sketch, "E8.31.1", {"start": v(64.7, -84.8) * mm, "mid": v(65.94, -85.52) * mm, "end": v(67.33, -85.94) * mm});
            skArc(sketch, "E8.31.2", {"start": v(55.7, -86.4) * mm, "mid": v(56.18, -84.59) * mm, "end": v(57.43, -83.2) * mm});
            skArc(sketch, "E8.31.3", {"start": v(56.36, -90.56) * mm, "mid": v(56.58, -91.99) * mm, "end": v(56.48, -93.43) * mm});
            skArc(sketch, "E8.31.4", {"start": v(61.03, -82.7) * mm, "mid": v(59.17, -82.52) * mm, "end": v(57.43, -83.2) * mm});
            skArc(sketch, "E8.31.5", {"start": v(56.04, -89.43) * mm, "mid": v(55.76, -87.92) * mm, "end": v(55.7, -86.4) * mm});
            skLineSegment(sketch, "E8.31.6", {"start": v(63.74, -84.11) * mm, "end": v(64.7, -84.8) * mm});
            skLineSegment(sketch, "E8.31.7", {"start": v(56.04, -89.43) * mm, "end": v(56.36, -90.56) * mm});
            skArc(sketch, "E8.32.0", {"start": v(73.42, -75.82) * mm, "mid": v(72.03, -75.18) * mm, "end": v(70.55, -74.75) * mm});
            skArc(sketch, "E8.32.1", {"start": v(74.44, -76.4) * mm, "mid": v(75.77, -76.95) * mm, "end": v(77.2, -77.2) * mm});
            skArc(sketch, "E8.32.2", {"start": v(65.7, -79.05) * mm, "mid": v(65.96, -77.2) * mm, "end": v(67.04, -75.67) * mm});
            skArc(sketch, "E8.32.3", {"start": v(66.86, -83.1) * mm, "mid": v(67.25, -84.5) * mm, "end": v(67.33, -85.94) * mm});
            skArc(sketch, "E8.32.4", {"start": v(70.55, -74.75) * mm, "mid": v(68.68, -74.79) * mm, "end": v(67.04, -75.67) * mm});
            skArc(sketch, "E8.32.5", {"start": v(66.41, -82.02) * mm, "mid": v(65.95, -80.56) * mm, "end": v(65.7, -79.05) * mm});
            skLineSegment(sketch, "E8.32.6", {"start": v(73.42, -75.82) * mm, "end": v(74.44, -76.4) * mm});
            skLineSegment(sketch, "E8.32.7", {"start": v(66.41, -82.02) * mm, "end": v(66.86, -83.1) * mm});
            skArc(sketch, "E8.33.0", {"start": v(82.02, -66.41) * mm, "mid": v(80.56, -65.95) * mm, "end": v(79.05, -65.7) * mm});
            skArc(sketch, "E8.33.1", {"start": v(83.1, -66.86) * mm, "mid": v(84.5, -67.25) * mm, "end": v(85.94, -67.33) * mm});
            skArc(sketch, "E8.33.2", {"start": v(74.75, -70.55) * mm, "mid": v(74.79, -68.68) * mm, "end": v(75.67, -67.04) * mm});
            skArc(sketch, "E8.33.3", {"start": v(76.4, -74.44) * mm, "mid": v(76.95, -75.77) * mm, "end": v(77.2, -77.2) * mm});
            skArc(sketch, "E8.33.4", {"start": v(79.05, -65.7) * mm, "mid": v(77.2, -65.96) * mm, "end": v(75.67, -67.04) * mm});
            skArc(sketch, "E8.33.5", {"start": v(75.82, -73.42) * mm, "mid": v(75.18, -72.03) * mm, "end": v(74.75, -70.55) * mm});
            skLineSegment(sketch, "E8.33.6", {"start": v(82.02, -66.41) * mm, "end": v(83.1, -66.86) * mm});
            skLineSegment(sketch, "E8.33.7", {"start": v(75.82, -73.42) * mm, "end": v(76.4, -74.44) * mm});
            skArc(sketch, "E8.34.0", {"start": v(89.43, -56.04) * mm, "mid": v(87.92, -55.76) * mm, "end": v(86.4, -55.7) * mm});
            skArc(sketch, "E8.34.1", {"start": v(90.56, -56.36) * mm, "mid": v(91.99, -56.58) * mm, "end": v(93.43, -56.48) * mm});
            skArc(sketch, "E8.34.2", {"start": v(82.7, -61.03) * mm, "mid": v(82.52, -59.17) * mm, "end": v(83.2, -57.43) * mm});
            skArc(sketch, "E8.34.3", {"start": v(84.8, -64.7) * mm, "mid": v(85.52, -65.94) * mm, "end": v(85.94, -67.33) * mm});
            skArc(sketch, "E8.34.4", {"start": v(86.4, -55.7) * mm, "mid": v(84.59, -56.18) * mm, "end": v(83.2, -57.43) * mm});
            skArc(sketch, "E8.34.5", {"start": v(84.11, -63.74) * mm, "mid": v(83.31, -62.44) * mm, "end": v(82.7, -61.03) * mm});
            skLineSegment(sketch, "E8.34.6", {"start": v(89.43, -56.04) * mm, "end": v(90.56, -56.36) * mm});
            skLineSegment(sketch, "E8.34.7", {"start": v(84.11, -63.74) * mm, "end": v(84.8, -64.7) * mm});
            skArc(sketch, "E8.35.0", {"start": v(95.53, -44.86) * mm, "mid": v(94, -44.75) * mm, "end": v(92.48, -44.87) * mm});
            skArc(sketch, "E8.35.1", {"start": v(96.7, -45.03) * mm, "mid": v(98.13, -45.08) * mm, "end": v(99.55, -44.8) * mm});
            skArc(sketch, "E8.35.2", {"start": v(89.46, -50.61) * mm, "mid": v(89.05, -48.8) * mm, "end": v(89.51, -46.98) * mm});
            skArc(sketch, "E8.35.3", {"start": v(91.99, -54) * mm, "mid": v(92.85, -55.16) * mm, "end": v(93.43, -56.48) * mm});
            skArc(sketch, "E8.35.4", {"start": v(92.48, -44.87) * mm, "mid": v(90.74, -45.57) * mm, "end": v(89.51, -46.98) * mm});
            skArc(sketch, "E8.35.5", {"start": v(91.18, -53.14) * mm, "mid": v(90.23, -51.94) * mm, "end": v(89.46, -50.61) * mm});
            skLineSegment(sketch, "E8.35.6", {"start": v(95.53, -44.86) * mm, "end": v(96.7, -45.03) * mm});
            skLineSegment(sketch, "E8.35.7", {"start": v(91.18, -53.14) * mm, "end": v(91.99, -54) * mm});
            skArc(sketch, "E8.36.0", {"start": v(100.24, -33.01) * mm, "mid": v(98.71, -33.1) * mm, "end": v(97.21, -33.4) * mm});
            skArc(sketch, "E8.36.1", {"start": v(101.42, -33.05) * mm, "mid": v(102.85, -32.92) * mm, "end": v(104.23, -32.48) * mm});
            skArc(sketch, "E8.36.2", {"start": v(94.91, -39.46) * mm, "mid": v(94.28, -37.7) * mm, "end": v(94.52, -35.85) * mm});
            skArc(sketch, "E8.36.3", {"start": v(97.82, -42.52) * mm, "mid": v(98.82, -43.56) * mm, "end": v(99.55, -44.8) * mm});
            skArc(sketch, "E8.36.4", {"start": v(97.21, -33.4) * mm, "mid": v(95.57, -34.3) * mm, "end": v(94.52, -35.85) * mm});
            skArc(sketch, "E8.36.5", {"start": v(96.92, -41.76) * mm, "mid": v(95.83, -40.69) * mm, "end": v(94.91, -39.46) * mm});
            skLineSegment(sketch, "E8.36.6", {"start": v(100.24, -33.01) * mm, "end": v(101.42, -33.05) * mm});
            skLineSegment(sketch, "E8.36.7", {"start": v(96.92, -41.76) * mm, "end": v(97.82, -42.52) * mm});
            skArc(sketch, "E8.37.0", {"start": v(103.5, -20.7) * mm, "mid": v(101.98, -20.96) * mm, "end": v(100.53, -21.44) * mm});
            skArc(sketch, "E8.37.1", {"start": v(104.66, -20.58) * mm, "mid": v(106.07, -20.28) * mm, "end": v(107.38, -19.68) * mm});
            skArc(sketch, "E8.37.2", {"start": v(98.98, -27.73) * mm, "mid": v(98.14, -26.06) * mm, "end": v(98.15, -24.2) * mm});
            skArc(sketch, "E8.37.3", {"start": v(102.23, -30.41) * mm, "mid": v(103.35, -31.33) * mm, "end": v(104.23, -32.48) * mm});
            skArc(sketch, "E8.37.4", {"start": v(100.53, -21.44) * mm, "mid": v(99.01, -22.53) * mm, "end": v(98.15, -24.2) * mm});
            skArc(sketch, "E8.37.5", {"start": v(101.25, -29.77) * mm, "mid": v(100.04, -28.84) * mm, "end": v(98.98, -27.73) * mm});
            skLineSegment(sketch, "E8.37.6", {"start": v(103.5, -20.7) * mm, "end": v(104.66, -20.58) * mm});
            skLineSegment(sketch, "E8.37.7", {"start": v(101.25, -29.77) * mm, "end": v(102.23, -30.41) * mm});
            skArc(sketch, "E8.38.0", {"start": v(105.23, -8.07) * mm, "mid": v(103.76, -8.5) * mm, "end": v(102.38, -9.17) * mm});
            skArc(sketch, "E8.38.1", {"start": v(106.38, -7.81) * mm, "mid": v(107.74, -7.35) * mm, "end": v(108.97, -6.6) * mm});
            skArc(sketch, "E8.38.2", {"start": v(101.6, -15.6) * mm, "mid": v(100.57, -14.04) * mm, "end": v(100.35, -12.19) * mm});
            skArc(sketch, "E8.38.3", {"start": v(105.16, -17.87) * mm, "mid": v(106.37, -18.65) * mm, "end": v(107.38, -19.68) * mm});
            skArc(sketch, "E8.38.4", {"start": v(102.38, -9.17) * mm, "mid": v(101, -10.43) * mm, "end": v(100.35, -12.19) * mm});
            skArc(sketch, "E8.38.5", {"start": v(104.1, -17.35) * mm, "mid": v(102.79, -16.57) * mm, "end": v(101.6, -15.6) * mm});
            skLineSegment(sketch, "E8.38.6", {"start": v(105.23, -8.07) * mm, "end": v(106.38, -7.81) * mm});
            skLineSegment(sketch, "E8.38.7", {"start": v(104.1, -17.35) * mm, "end": v(105.16, -17.87) * mm});
            skArc(sketch, "E8.39.0", {"start": v(105.43, 4.68) * mm, "mid": v(104.03, 4.06) * mm, "end": v(102.74, 3.24) * mm});
            skArc(sketch, "E8.39.1", {"start": v(106.54, 5.06) * mm, "mid": v(107.84, 5.7) * mm, "end": v(108.97, 6.6) * mm});
            skArc(sketch, "E8.39.2", {"start": v(102.74, -3.24) * mm, "mid": v(101.53, -1.82) * mm, "end": v(101.1, 0) * mm});
            skArc(sketch, "E8.39.3", {"start": v(106.54, -5.06) * mm, "mid": v(107.84, -5.7) * mm, "end": v(108.97, -6.6) * mm});
            skArc(sketch, "E8.39.4", {"start": v(102.74, 3.24) * mm, "mid": v(101.53, 1.82) * mm, "end": v(101.1, 0) * mm});
            skArc(sketch, "E8.39.5", {"start": v(105.43, -4.68) * mm, "mid": v(104.03, -4.06) * mm, "end": v(102.74, -3.24) * mm});
            skLineSegment(sketch, "E8.39.6", {"start": v(105.43, 4.68) * mm, "end": v(106.54, 5.06) * mm});
            skLineSegment(sketch, "E8.39.7", {"start": v(105.43, -4.68) * mm, "end": v(106.54, -5.06) * mm});
            skArc(sketch, "E8.40.0", {"start": v(104.1, 17.35) * mm, "mid": v(102.79, 16.57) * mm, "end": v(101.6, 15.6) * mm});
            skArc(sketch, "E8.40.1", {"start": v(105.16, 17.87) * mm, "mid": v(106.37, 18.65) * mm, "end": v(107.38, 19.68) * mm});
            skArc(sketch, "E8.40.2", {"start": v(102.38, 9.17) * mm, "mid": v(101, 10.43) * mm, "end": v(100.35, 12.19) * mm});
            skArc(sketch, "E8.40.3", {"start": v(106.38, 7.81) * mm, "mid": v(107.74, 7.35) * mm, "end": v(108.97, 6.6) * mm});
            skArc(sketch, "E8.40.4", {"start": v(101.6, 15.6) * mm, "mid": v(100.57, 14.04) * mm, "end": v(100.35, 12.19) * mm});
            skArc(sketch, "E8.40.5", {"start": v(105.23, 8.07) * mm, "mid": v(103.76, 8.5) * mm, "end": v(102.38, 9.17) * mm});
            skLineSegment(sketch, "E8.40.6", {"start": v(104.1, 17.35) * mm, "end": v(105.16, 17.87) * mm});
            skLineSegment(sketch, "E8.40.7", {"start": v(105.23, 8.07) * mm, "end": v(106.38, 7.81) * mm});
            skArc(sketch, "E8.41.0", {"start": v(101.25, 29.77) * mm, "mid": v(100.04, 28.84) * mm, "end": v(98.98, 27.73) * mm});
            skArc(sketch, "E8.41.1", {"start": v(102.23, 30.41) * mm, "mid": v(103.35, 31.33) * mm, "end": v(104.23, 32.48) * mm});
            skArc(sketch, "E8.41.2", {"start": v(100.53, 21.44) * mm, "mid": v(99.01, 22.53) * mm, "end": v(98.15, 24.2) * mm});
            skArc(sketch, "E8.41.3", {"start": v(104.66, 20.58) * mm, "mid": v(106.07, 20.28) * mm, "end": v(107.38, 19.68) * mm});
            skArc(sketch, "E8.41.4", {"start": v(98.98, 27.73) * mm, "mid": v(98.14, 26.06) * mm, "end": v(98.15, 24.2) * mm});
            skArc(sketch, "E8.41.5", {"start": v(103.5, 20.7) * mm, "mid": v(101.98, 20.96) * mm, "end": v(100.53, 21.44) * mm});
            skLineSegment(sketch, "E8.41.6", {"start": v(101.25, 29.77) * mm, "end": v(102.23, 30.41) * mm});
            skLineSegment(sketch, "E8.41.7", {"start": v(103.5, 20.7) * mm, "end": v(104.66, 20.58) * mm});
            skArc(sketch, "E8.42.0", {"start": v(96.92, 41.76) * mm, "mid": v(95.83, 40.69) * mm, "end": v(94.91, 39.46) * mm});
            skArc(sketch, "E8.42.1", {"start": v(97.82, 42.52) * mm, "mid": v(98.82, 43.56) * mm, "end": v(99.55, 44.8) * mm});
            skArc(sketch, "E8.42.2", {"start": v(97.21, 33.4) * mm, "mid": v(95.57, 34.3) * mm, "end": v(94.52, 35.85) * mm});
            skArc(sketch, "E8.42.3", {"start": v(101.42, 33.05) * mm, "mid": v(102.85, 32.92) * mm, "end": v(104.23, 32.48) * mm});
            skArc(sketch, "E8.42.4", {"start": v(94.91, 39.46) * mm, "mid": v(94.28, 37.7) * mm, "end": v(94.52, 35.85) * mm});
            skArc(sketch, "E8.42.5", {"start": v(100.24, 33.01) * mm, "mid": v(98.71, 33.1) * mm, "end": v(97.21, 33.4) * mm});
            skLineSegment(sketch, "E8.42.6", {"start": v(96.92, 41.76) * mm, "end": v(97.82, 42.52) * mm});
            skLineSegment(sketch, "E8.42.7", {"start": v(100.24, 33.01) * mm, "end": v(101.42, 33.05) * mm});
            skArc(sketch, "E8.43.0", {"start": v(91.18, 53.14) * mm, "mid": v(90.23, 51.94) * mm, "end": v(89.46, 50.61) * mm});
            skArc(sketch, "E8.43.1", {"start": v(91.99, 54) * mm, "mid": v(92.85, 55.16) * mm, "end": v(93.43, 56.48) * mm});
            skArc(sketch, "E8.43.2", {"start": v(92.48, 44.87) * mm, "mid": v(90.74, 45.57) * mm, "end": v(89.51, 46.98) * mm});
            skArc(sketch, "E8.43.3", {"start": v(96.7, 45.03) * mm, "mid": v(98.13, 45.08) * mm, "end": v(99.55, 44.8) * mm});
            skArc(sketch, "E8.43.4", {"start": v(89.46, 50.61) * mm, "mid": v(89.05, 48.8) * mm, "end": v(89.51, 46.98) * mm});
            skArc(sketch, "E8.43.5", {"start": v(95.53, 44.86) * mm, "mid": v(94, 44.75) * mm, "end": v(92.48, 44.87) * mm});
            skLineSegment(sketch, "E8.43.6", {"start": v(91.18, 53.14) * mm, "end": v(91.99, 54) * mm});
            skLineSegment(sketch, "E8.43.7", {"start": v(95.53, 44.86) * mm, "end": v(96.7, 45.03) * mm});
            skArc(sketch, "E8.44.0", {"start": v(84.11, 63.74) * mm, "mid": v(83.31, 62.44) * mm, "end": v(82.7, 61.03) * mm});
            skArc(sketch, "E8.44.1", {"start": v(84.8, 64.7) * mm, "mid": v(85.52, 65.94) * mm, "end": v(85.94, 67.33) * mm});
            skArc(sketch, "E8.44.2", {"start": v(86.4, 55.7) * mm, "mid": v(84.59, 56.18) * mm, "end": v(83.2, 57.43) * mm});
            skArc(sketch, "E8.44.3", {"start": v(90.56, 56.36) * mm, "mid": v(91.99, 56.58) * mm, "end": v(93.43, 56.48) * mm});
            skArc(sketch, "E8.44.4", {"start": v(82.7, 61.03) * mm, "mid": v(82.52, 59.17) * mm, "end": v(83.2, 57.43) * mm});
            skArc(sketch, "E8.44.5", {"start": v(89.43, 56.04) * mm, "mid": v(87.92, 55.76) * mm, "end": v(86.4, 55.7) * mm});
            skLineSegment(sketch, "E8.44.6", {"start": v(84.11, 63.74) * mm, "end": v(84.8, 64.7) * mm});
            skLineSegment(sketch, "E8.44.7", {"start": v(89.43, 56.04) * mm, "end": v(90.56, 56.36) * mm});
            skArc(sketch, "E8.45.0", {"start": v(75.82, 73.42) * mm, "mid": v(75.18, 72.03) * mm, "end": v(74.75, 70.55) * mm});
            skArc(sketch, "E8.45.1", {"start": v(76.4, 74.44) * mm, "mid": v(76.95, 75.77) * mm, "end": v(77.2, 77.2) * mm});
            skArc(sketch, "E8.45.2", {"start": v(79.05, 65.7) * mm, "mid": v(77.2, 65.96) * mm, "end": v(75.67, 67.04) * mm});
            skArc(sketch, "E8.45.3", {"start": v(83.1, 66.86) * mm, "mid": v(84.5, 67.25) * mm, "end": v(85.94, 67.33) * mm});
            skArc(sketch, "E8.45.4", {"start": v(74.75, 70.55) * mm, "mid": v(74.79, 68.68) * mm, "end": v(75.67, 67.04) * mm});
            skArc(sketch, "E8.45.5", {"start": v(82.02, 66.41) * mm, "mid": v(80.56, 65.95) * mm, "end": v(79.05, 65.7) * mm});
            skLineSegment(sketch, "E8.45.6", {"start": v(75.82, 73.42) * mm, "end": v(76.4, 74.44) * mm});
            skLineSegment(sketch, "E8.45.7", {"start": v(82.02, 66.41) * mm, "end": v(83.1, 66.86) * mm});
            skArc(sketch, "E8.46.0", {"start": v(66.41, 82.02) * mm, "mid": v(65.95, 80.56) * mm, "end": v(65.7, 79.05) * mm});
            skArc(sketch, "E8.46.1", {"start": v(66.86, 83.1) * mm, "mid": v(67.25, 84.5) * mm, "end": v(67.33, 85.94) * mm});
            skArc(sketch, "E8.46.2", {"start": v(70.55, 74.75) * mm, "mid": v(68.68, 74.79) * mm, "end": v(67.04, 75.67) * mm});
            skArc(sketch, "E8.46.3", {"start": v(74.44, 76.4) * mm, "mid": v(75.77, 76.95) * mm, "end": v(77.2, 77.2) * mm});
            skArc(sketch, "E8.46.4", {"start": v(65.7, 79.05) * mm, "mid": v(65.96, 77.2) * mm, "end": v(67.04, 75.67) * mm});
            skArc(sketch, "E8.46.5", {"start": v(73.42, 75.82) * mm, "mid": v(72.03, 75.18) * mm, "end": v(70.55, 74.75) * mm});
            skLineSegment(sketch, "E8.46.6", {"start": v(66.41, 82.02) * mm, "end": v(66.86, 83.1) * mm});
            skLineSegment(sketch, "E8.46.7", {"start": v(73.42, 75.82) * mm, "end": v(74.44, 76.4) * mm});
            skArc(sketch, "E8.47.0", {"start": v(56.04, 89.43) * mm, "mid": v(55.76, 87.92) * mm, "end": v(55.7, 86.4) * mm});
            skArc(sketch, "E8.47.1", {"start": v(56.36, 90.56) * mm, "mid": v(56.58, 91.99) * mm, "end": v(56.48, 93.43) * mm});
            skArc(sketch, "E8.47.2", {"start": v(61.03, 82.7) * mm, "mid": v(59.17, 82.52) * mm, "end": v(57.43, 83.2) * mm});
            skArc(sketch, "E8.47.3", {"start": v(64.7, 84.8) * mm, "mid": v(65.94, 85.52) * mm, "end": v(67.33, 85.94) * mm});
            skArc(sketch, "E8.47.4", {"start": v(55.7, 86.4) * mm, "mid": v(56.18, 84.59) * mm, "end": v(57.43, 83.2) * mm});
            skArc(sketch, "E8.47.5", {"start": v(63.74, 84.11) * mm, "mid": v(62.44, 83.31) * mm, "end": v(61.03, 82.7) * mm});
            skLineSegment(sketch, "E8.47.6", {"start": v(56.04, 89.43) * mm, "end": v(56.36, 90.56) * mm});
            skLineSegment(sketch, "E8.47.7", {"start": v(63.74, 84.11) * mm, "end": v(64.7, 84.8) * mm});
            skArc(sketch, "E8.48.0", {"start": v(44.86, 95.53) * mm, "mid": v(44.75, 94) * mm, "end": v(44.87, 92.48) * mm});
            skArc(sketch, "E8.48.1", {"start": v(45.03, 96.7) * mm, "mid": v(45.08, 98.13) * mm, "end": v(44.8, 99.55) * mm});
            skArc(sketch, "E8.48.2", {"start": v(50.61, 89.46) * mm, "mid": v(48.8, 89.05) * mm, "end": v(46.98, 89.51) * mm});
            skArc(sketch, "E8.48.3", {"start": v(54, 91.99) * mm, "mid": v(55.16, 92.85) * mm, "end": v(56.48, 93.43) * mm});
            skArc(sketch, "E8.48.4", {"start": v(44.87, 92.48) * mm, "mid": v(45.57, 90.74) * mm, "end": v(46.98, 89.51) * mm});
            skArc(sketch, "E8.48.5", {"start": v(53.14, 91.18) * mm, "mid": v(51.94, 90.23) * mm, "end": v(50.61, 89.46) * mm});
            skLineSegment(sketch, "E8.48.6", {"start": v(44.86, 95.53) * mm, "end": v(45.03, 96.7) * mm});
            skLineSegment(sketch, "E8.48.7", {"start": v(53.14, 91.18) * mm, "end": v(54, 91.99) * mm});
            skArc(sketch, "E8.49.0", {"start": v(33.01, 100.24) * mm, "mid": v(33.1, 98.71) * mm, "end": v(33.4, 97.21) * mm});
            skArc(sketch, "E8.49.1", {"start": v(33.05, 101.42) * mm, "mid": v(32.92, 102.85) * mm, "end": v(32.48, 104.23) * mm});
            skArc(sketch, "E8.49.2", {"start": v(39.46, 94.91) * mm, "mid": v(37.7, 94.28) * mm, "end": v(35.85, 94.52) * mm});
            skArc(sketch, "E8.49.3", {"start": v(42.52, 97.82) * mm, "mid": v(43.56, 98.82) * mm, "end": v(44.8, 99.55) * mm});
            skArc(sketch, "E8.49.4", {"start": v(33.4, 97.21) * mm, "mid": v(34.3, 95.57) * mm, "end": v(35.85, 94.52) * mm});
            skArc(sketch, "E8.49.5", {"start": v(41.76, 96.92) * mm, "mid": v(40.69, 95.83) * mm, "end": v(39.46, 94.91) * mm});
            skLineSegment(sketch, "E8.49.6", {"start": v(33.01, 100.24) * mm, "end": v(33.05, 101.42) * mm});
            skLineSegment(sketch, "E8.49.7", {"start": v(41.76, 96.92) * mm, "end": v(42.52, 97.82) * mm});
            skArc(sketch, "E8.50.0", {"start": v(20.7, 103.5) * mm, "mid": v(20.96, 101.98) * mm, "end": v(21.44, 100.53) * mm});
            skArc(sketch, "E8.50.1", {"start": v(20.58, 104.66) * mm, "mid": v(20.28, 106.07) * mm, "end": v(19.68, 107.38) * mm});
            skArc(sketch, "E8.50.2", {"start": v(27.73, 98.98) * mm, "mid": v(26.06, 98.14) * mm, "end": v(24.2, 98.15) * mm});
            skArc(sketch, "E8.50.3", {"start": v(30.41, 102.23) * mm, "mid": v(31.33, 103.35) * mm, "end": v(32.48, 104.23) * mm});
            skArc(sketch, "E8.50.4", {"start": v(21.44, 100.53) * mm, "mid": v(22.53, 99.01) * mm, "end": v(24.2, 98.15) * mm});
            skArc(sketch, "E8.50.5", {"start": v(29.77, 101.25) * mm, "mid": v(28.84, 100.04) * mm, "end": v(27.73, 98.98) * mm});
            skLineSegment(sketch, "E8.50.6", {"start": v(20.7, 103.5) * mm, "end": v(20.58, 104.66) * mm});
            skLineSegment(sketch, "E8.50.7", {"start": v(29.77, 101.25) * mm, "end": v(30.41, 102.23) * mm});
            skArc(sketch, "E8.51.0", {"start": v(8.07, 105.23) * mm, "mid": v(8.5, 103.76) * mm, "end": v(9.17, 102.38) * mm});
            skArc(sketch, "E8.51.1", {"start": v(7.81, 106.38) * mm, "mid": v(7.35, 107.74) * mm, "end": v(6.6, 108.97) * mm});
            skArc(sketch, "E8.51.2", {"start": v(15.6, 101.6) * mm, "mid": v(14.04, 100.57) * mm, "end": v(12.19, 100.35) * mm});
            skArc(sketch, "E8.51.3", {"start": v(17.87, 105.16) * mm, "mid": v(18.65, 106.37) * mm, "end": v(19.68, 107.38) * mm});
            skArc(sketch, "E8.51.4", {"start": v(9.17, 102.38) * mm, "mid": v(10.43, 101) * mm, "end": v(12.19, 100.35) * mm});
            skArc(sketch, "E8.51.5", {"start": v(17.35, 104.1) * mm, "mid": v(16.57, 102.79) * mm, "end": v(15.6, 101.6) * mm});
            skLineSegment(sketch, "E8.51.6", {"start": v(8.07, 105.23) * mm, "end": v(7.81, 106.38) * mm});
            skLineSegment(sketch, "E8.51.7", {"start": v(17.35, 104.1) * mm, "end": v(17.87, 105.16) * mm});
            skPoint(sketch, "E8.center", {"position": v(0, 0) * mm});
            skCircle(sketch, "E9", {"center": v(0, 0) * mm, "radius": 107.55 * mm});
            skCircle(sketch, "E10", {"center": v(0, 0) * mm, "radius": 98.6 * mm});
            skCircle(sketch, "E11", {"center": v(0, 0) * mm, "radius": 65 * mm});
            skCircle(sketch, "E12", {"center": v(0, 72) * mm, "radius": 5.25 * mm});
            skCircle(sketch, "E13.1.0", {"center": v(-68.48, 22.25) * mm, "radius": 5.25 * mm});
            skCircle(sketch, "E13.2.0", {"center": v(-42.32, -58.25) * mm, "radius": 5.25 * mm});
            skCircle(sketch, "E13.3.0", {"center": v(42.32, -58.25) * mm, "radius": 5.25 * mm});
            skCircle(sketch, "E13.4.0", {"center": v(68.48, 22.25) * mm, "radius": 5.25 * mm});
            skSolve(sketch);
        }
        {
            var Q0;
            Q0=makeQuery(id+"F0.imprint","IMPRINT",FACE,{"disambiguationData":[TD([[makeQuery(id+"F0.imprint","IMPRINT",EDGE,{"derivedFrom":sQuery(id+"F0.wireOp",EDGE,"E0")}),-1.0]])]});
            extrude(context, id + "F1", {"entities" : qUnion([Q0]), "endBound" : BoundingType.SYMMETRIC, "depth" : 3.2 * mm});
        }
        {
            var Q0;
            Q0=makeQuery(id+"F0.imprint","IMPRINT",FACE,{"disambiguationData":[TD([[makeQuery(id+"F0.imprint","IMPRINT",EDGE,{"derivedFrom":sQuery(id+"F0.wireOp",EDGE,"E10")}),1.0]])]});
            extrude(context, id + "F2", {"entities" : qUnion([Q0]), "operationType" : NewBodyOperationType.ADD, "endBound" : BoundingType.SYMMETRIC, "depth" : 4.5 * mm});
        }
        {
            var Q0;
            Q0=makeQuery(id+"F2.opExtrude","CAP_FACE",FACE,{"disambiguationData":[OSD([sQuery(id+"F0.wireOp",EDGE,"E10"),sQuery(id+"F0.wireOp",EDGE,"E11"),sQuery(id+"F0.wireOp",EDGE,"E12"),sQuery(id+"F0.wireOp",EDGE,"E13.1.0"),sQuery(id+"F0.wireOp",EDGE,"E13.2.0"),sQuery(id+"F0.wireOp",EDGE,"E13.3.0"),sQuery(id+"F0.wireOp",EDGE,"E13.4.0")])],"isStart":false});
            var sketch = newSketch(context, id + "F3", { "sketchPlane" : qUnion([Q0])});
            skLineSegment(sketch, "E14", {"start": v(71.01, 12.2) * mm, "end": v(90.17, 15.5) * mm});
            skLineSegment(sketch, "E15", {"start": v(50.28, -51.61) * mm, "end": v(63.84, -65.53) * mm});
            skArc(sketch, "E16", {"start": v(50.27, -48.82) * mm, "mid": v(52.28, -46.66) * mm, "end": v(54.2, -44.42) * mm});
            skArc(sketch, "E17", {"start": v(66.7, -65.54) * mm, "mid": v(69.76, -62.27) * mm, "end": v(72.67, -58.85) * mm});
            skLineSegment(sketch, "E18", {"start": v(72.02, 2.2) * mm, "end": v(91.45, 2.8) * mm});
            skLineSegment(sketch, "E19", {"start": v(72.05, 0.32) * mm, "end": v(91.49, 0.4) * mm});
            skLineSegment(sketch, "E20", {"start": v(71.4, -9.71) * mm, "end": v(90.65, -12.34) * mm});
            skLineSegment(sketch, "E21", {"start": v(71.12, -11.58) * mm, "end": v(90.3, -14.7) * mm});
            skArc(sketch, "E22.trimOffspring", {"start": v(69.96, 4.08) * mm, "mid": v(69.73, 7.02) * mm, "end": v(69.37, 9.95) * mm});
            skArc(sketch, "E23.trimOffspring", {"start": v(93.38, 4.9) * mm, "mid": v(93.04, 9.37) * mm, "end": v(92.48, 13.82) * mm});
            skArc(sketch, "E24.trimOffspring", {"start": v(92.91, -10.58) * mm, "mid": v(93.31, -6.11) * mm, "end": v(93.5, -1.63) * mm});
            skArc(sketch, "E25.trimOffspring", {"start": v(69.68, -7.52) * mm, "mid": v(69.93, -4.58) * mm, "end": v(70.06, -1.64) * mm});
            skLineSegment(sketch, "E26", {"start": v(68.81, -21.37) * mm, "end": v(87.37, -27.13) * mm});
            skLineSegment(sketch, "E27", {"start": v(68.23, -23.16) * mm, "end": v(86.63, -29.4) * mm});
            skArc(sketch, "E28.trimOffspring", {"start": v(89.89, -25.77) * mm, "mid": v(91.02, -21.43) * mm, "end": v(91.94, -17.04) * mm});
            skArc(sketch, "E29.trimOffspring", {"start": v(67.48, -18.92) * mm, "mid": v(68.21, -16.06) * mm, "end": v(68.83, -13.18) * mm});
            skLineSegment(sketch, "E30", {"start": v(64.34, -32.43) * mm, "end": v(81.7, -41.18) * mm});
            skLineSegment(sketch, "E31", {"start": v(63.47, -34.1) * mm, "end": v(80.6, -43.3) * mm});
            skArc(sketch, "E32.trimOffspring", {"start": v(63.43, -29.8) * mm, "mid": v(64.63, -27.1) * mm, "end": v(65.71, -24.36) * mm});
            skArc(sketch, "E33.trimOffspring", {"start": v(84.4, -40.25) * mm, "mid": v(86.24, -36.16) * mm, "end": v(87.87, -31.98) * mm});
            skLineSegment(sketch, "E34", {"start": v(58.1, -42.6) * mm, "end": v(73.78, -54.1) * mm});
            skLineSegment(sketch, "E35", {"start": v(56.97, -44.11) * mm, "end": v(72.34, -56) * mm});
            skArc(sketch, "E36.trimOffspring", {"start": v(76.6, -53.63) * mm, "mid": v(79.09, -49.9) * mm, "end": v(81.39, -46.05) * mm});
            skArc(sketch, "E37.trimOffspring", {"start": v(57.64, -39.85) * mm, "mid": v(59.27, -37.4) * mm, "end": v(60.79, -34.87) * mm});
            skArc(sketch, "E38.1.0", {"start": v(24.2, 90.33) * mm, "mid": v(19.84, 91.38) * mm, "end": v(15.44, 92.23) * mm});
            skLineSegment(sketch, "E38.1.1", {"start": v(41.58, 58.84) * mm, "end": v(52.8, 74.71) * mm});
            skArc(sketch, "E38.1.2", {"start": v(28.68, 63.94) * mm, "mid": v(25.97, 65.1) * mm, "end": v(23.2, 66.13) * mm});
            skLineSegment(sketch, "E38.1.3", {"start": v(58.47, 42.1) * mm, "end": v(74.25, 53.45) * mm});
            skLineSegment(sketch, "E38.1.4", {"start": v(50.72, 51.17) * mm, "end": v(64.4, 64.98) * mm});
            skArc(sketch, "E38.1.5", {"start": v(38.77, 85.1) * mm, "mid": v(34.65, 86.85) * mm, "end": v(30.45, 88.42) * mm});
            skArc(sketch, "E38.1.6", {"start": v(17.73, 67.8) * mm, "mid": v(14.87, 68.48) * mm, "end": v(11.98, 69.05) * mm});
            skArc(sketch, "E38.1.7", {"start": v(38.84, 58.33) * mm, "mid": v(36.35, 59.91) * mm, "end": v(33.8, 61.39) * mm});
            skLineSegment(sketch, "E38.1.8", {"start": v(32.99, 64.06) * mm, "end": v(41.89, 81.34) * mm});
            skLineSegment(sketch, "E38.1.9", {"start": v(52.05, 49.83) * mm, "end": v(66.09, 63.27) * mm});
            skArc(sketch, "E38.1.10", {"start": v(82.94, 43.18) * mm, "mid": v(80.78, 47.1) * mm, "end": v(78.43, 50.93) * mm});
            skArc(sketch, "E38.1.11", {"start": v(74.68, 56.28) * mm, "mid": v(71.9, 59.8) * mm, "end": v(68.94, 63.17) * mm});
            skArc(sketch, "E38.1.12", {"start": v(47.94, 51.12) * mm, "mid": v(45.74, 53.1) * mm, "end": v(43.47, 54.97) * mm});
            skLineSegment(sketch, "E38.1.13", {"start": v(59.56, 40.55) * mm, "end": v(75.62, 51.5) * mm});
            skLineSegment(sketch, "E38.1.14", {"start": v(10.34, 71.3) * mm, "end": v(13.13, 90.54) * mm});
            skLineSegment(sketch, "E38.1.15", {"start": v(31.3, 64.9) * mm, "end": v(39.75, 82.4) * mm});
            skLineSegment(sketch, "E38.1.16", {"start": v(20.16, 69.17) * mm, "end": v(25.6, 87.83) * mm});
            skArc(sketch, "E38.1.17", {"start": v(64.36, 67.83) * mm, "mid": v(61.04, 70.84) * mm, "end": v(57.57, 73.69) * mm});
            skLineSegment(sketch, "E38.1.18", {"start": v(21.96, 68.62) * mm, "end": v(27.89, 87.13) * mm});
            skLineSegment(sketch, "E38.1.19", {"start": v(64.62, 31.87) * mm, "end": v(82.05, 40.46) * mm});
            skArc(sketch, "E38.1.20", {"start": v(52.29, 77.53) * mm, "mid": v(48.5, 79.94) * mm, "end": v(44.62, 82.18) * mm});
            skLineSegment(sketch, "E38.1.21", {"start": v(43.1, 57.73) * mm, "end": v(54.74, 73.3) * mm});
            skArc(sketch, "E38.1.22", {"start": v(55.72, 42.5) * mm, "mid": v(53.88, 44.81) * mm, "end": v(51.95, 47.04) * mm});
            skArc(sketch, "E38.1.23", {"start": v(61.97, 32.73) * mm, "mid": v(60.54, 35.3) * mm, "end": v(59, 37.82) * mm});
            skArc(sketch, "E38.2.0", {"start": v(-78.43, 50.92) * mm, "mid": v(-80.78, 47.1) * mm, "end": v(-82.94, 43.18) * mm});
            skLineSegment(sketch, "E38.2.1", {"start": v(-43.11, 57.73) * mm, "end": v(-54.74, 73.3) * mm});
            skArc(sketch, "E38.2.2", {"start": v(-51.95, 47.04) * mm, "mid": v(-53.88, 44.81) * mm, "end": v(-55.72, 42.5) * mm});
            skLineSegment(sketch, "E38.2.3", {"start": v(-21.97, 68.62) * mm, "end": v(-27.9, 87.13) * mm});
            skLineSegment(sketch, "E38.2.4", {"start": v(-33, 64.06) * mm, "end": v(-41.9, 81.33) * mm});
            skArc(sketch, "E38.2.5", {"start": v(-68.95, 63.17) * mm, "mid": v(-71.9, 59.8) * mm, "end": v(-74.68, 56.28) * mm});
            skArc(sketch, "E38.2.6", {"start": v(-59, 37.82) * mm, "mid": v(-60.54, 35.3) * mm, "end": v(-61.97, 32.73) * mm});
            skArc(sketch, "E38.2.7", {"start": v(-43.47, 54.97) * mm, "mid": v(-45.75, 53.09) * mm, "end": v(-47.94, 51.12) * mm});
            skLineSegment(sketch, "E38.2.8", {"start": v(-50.73, 51.17) * mm, "end": v(-64.41, 64.97) * mm});
            skLineSegment(sketch, "E38.2.9", {"start": v(-31.3, 64.9) * mm, "end": v(-39.75, 82.4) * mm});
            skArc(sketch, "E38.2.10", {"start": v(-15.44, 92.23) * mm, "mid": v(-19.84, 91.38) * mm, "end": v(-24.2, 90.32) * mm});
            skArc(sketch, "E38.2.11", {"start": v(-30.45, 88.41) * mm, "mid": v(-34.65, 86.85) * mm, "end": v(-38.78, 85.1) * mm});
            skArc(sketch, "E38.2.12", {"start": v(-33.8, 61.39) * mm, "mid": v(-36.36, 59.91) * mm, "end": v(-38.84, 58.33) * mm});
            skLineSegment(sketch, "E38.2.13", {"start": v(-20.16, 69.17) * mm, "end": v(-25.6, 87.83) * mm});
            skLineSegment(sketch, "E38.2.14", {"start": v(-64.62, 31.87) * mm, "end": v(-82.05, 40.46) * mm});
            skLineSegment(sketch, "E38.2.15", {"start": v(-52.05, 49.82) * mm, "end": v(-66.09, 63.26) * mm});
            skLineSegment(sketch, "E38.2.16", {"start": v(-59.56, 40.55) * mm, "end": v(-75.62, 51.49) * mm});
            skArc(sketch, "E38.2.17", {"start": v(-44.62, 82.18) * mm, "mid": v(-48.51, 79.94) * mm, "end": v(-52.29, 77.52) * mm});
            skLineSegment(sketch, "E38.2.18", {"start": v(-58.48, 42.1) * mm, "end": v(-74.25, 53.45) * mm});
            skLineSegment(sketch, "E38.2.19", {"start": v(-10.34, 71.3) * mm, "end": v(-13.13, 90.54) * mm});
            skArc(sketch, "E38.2.20", {"start": v(-57.58, 73.68) * mm, "mid": v(-61.04, 70.84) * mm, "end": v(-64.37, 67.83) * mm});
            skLineSegment(sketch, "E38.2.21", {"start": v(-41.59, 58.84) * mm, "end": v(-52.8, 74.71) * mm});
            skArc(sketch, "E38.2.22", {"start": v(-23.2, 66.12) * mm, "mid": v(-25.97, 65.1) * mm, "end": v(-28.68, 63.94) * mm});
            skArc(sketch, "E38.2.23", {"start": v(-11.98, 69.05) * mm, "mid": v(-14.87, 68.48) * mm, "end": v(-17.74, 67.8) * mm});
            skArc(sketch, "E38.3.0", {"start": v(-72.67, -58.85) * mm, "mid": v(-69.76, -62.27) * mm, "end": v(-66.7, -65.54) * mm});
            skLineSegment(sketch, "E38.3.1", {"start": v(-68.23, -23.16) * mm, "end": v(-86.63, -29.4) * mm});
            skArc(sketch, "E38.3.2", {"start": v(-60.79, -34.87) * mm, "mid": v(-59.27, -37.4) * mm, "end": v(-57.64, -39.86) * mm});
            skLineSegment(sketch, "E38.3.3", {"start": v(-72.05, 0.31) * mm, "end": v(-91.49, 0.4) * mm});
            skLineSegment(sketch, "E38.3.4", {"start": v(-71.12, -11.58) * mm, "end": v(-90.3, -14.7) * mm});
            skArc(sketch, "E38.3.5", {"start": v(-81.38, -46.05) * mm, "mid": v(-79.08, -49.9) * mm, "end": v(-76.6, -53.63) * mm});
            skArc(sketch, "E38.3.6", {"start": v(-54.2, -44.43) * mm, "mid": v(-52.28, -46.67) * mm, "end": v(-50.27, -48.82) * mm});
            skArc(sketch, "E38.3.7", {"start": v(-65.7, -24.36) * mm, "mid": v(-64.63, -27.1) * mm, "end": v(-63.43, -29.8) * mm});
            skLineSegment(sketch, "E38.3.8", {"start": v(-64.34, -32.43) * mm, "end": v(-81.7, -41.18) * mm});
            skLineSegment(sketch, "E38.3.9", {"start": v(-71.4, -9.72) * mm, "end": v(-90.65, -12.34) * mm});
            skArc(sketch, "E38.3.10", {"start": v(-92.48, 13.82) * mm, "mid": v(-93.04, 9.37) * mm, "end": v(-93.38, 4.9) * mm});
            skArc(sketch, "E38.3.11", {"start": v(-93.5, -1.64) * mm, "mid": v(-93.31, -6.12) * mm, "end": v(-92.9, -10.58) * mm});
            skArc(sketch, "E38.3.12", {"start": v(-68.83, -13.18) * mm, "mid": v(-68.21, -16.06) * mm, "end": v(-67.48, -18.92) * mm});
            skLineSegment(sketch, "E38.3.13", {"start": v(-72.02, 2.2) * mm, "end": v(-91.45, 2.8) * mm});
            skLineSegment(sketch, "E38.3.14", {"start": v(-50.28, -51.61) * mm, "end": v(-63.84, -65.53) * mm});
            skLineSegment(sketch, "E38.3.15", {"start": v(-63.47, -34.1) * mm, "end": v(-80.6, -43.3) * mm});
            skLineSegment(sketch, "E38.3.16", {"start": v(-56.97, -44.11) * mm, "end": v(-72.34, -56.01) * mm});
            skArc(sketch, "E38.3.17", {"start": v(-91.94, -17.05) * mm, "mid": v(-91.02, -21.43) * mm, "end": v(-89.89, -25.77) * mm});
            skLineSegment(sketch, "E38.3.18", {"start": v(-58.1, -42.6) * mm, "end": v(-73.78, -54.1) * mm});
            skLineSegment(sketch, "E38.3.19", {"start": v(-71.01, 12.2) * mm, "end": v(-90.17, 15.5) * mm});
            skArc(sketch, "E38.3.20", {"start": v(-87.87, -31.99) * mm, "mid": v(-86.23, -36.16) * mm, "end": v(-84.4, -40.26) * mm});
            skLineSegment(sketch, "E38.3.21", {"start": v(-68.81, -21.37) * mm, "end": v(-87.37, -27.13) * mm});
            skArc(sketch, "E38.3.22", {"start": v(-70.06, -1.64) * mm, "mid": v(-69.93, -4.58) * mm, "end": v(-69.68, -7.52) * mm});
            skArc(sketch, "E38.3.23", {"start": v(-69.37, 9.95) * mm, "mid": v(-69.73, 7.02) * mm, "end": v(-69.96, 4.08) * mm});
            skPoint(sketch, "E39.visualSharp", {"position": v(65.25, -66.98) * mm});
            skArc(sketch, "E39.filletArc", {"start": v(63.84, -65.53) * mm, "mid": v(65.27, -66.14) * mm, "end": v(66.7, -65.54) * mm});
            skPoint(sketch, "E40.visualSharp", {"position": v(73.94, -57.25) * mm});
            skArc(sketch, "E40.filletArc", {"start": v(72.67, -58.85) * mm, "mid": v(73.1, -57.36) * mm, "end": v(72.34, -56) * mm});
            skPoint(sketch, "E41.visualSharp", {"position": v(75.41, -55.3) * mm});
            skArc(sketch, "E41.filletArc", {"start": v(73.78, -54.1) * mm, "mid": v(75.3, -54.46) * mm, "end": v(76.6, -53.63) * mm});
            skPoint(sketch, "E42.visualSharp", {"position": v(82.37, -44.26) * mm});
            skArc(sketch, "E42.filletArc", {"start": v(81.39, -46.05) * mm, "mid": v(81.57, -44.5) * mm, "end": v(80.6, -43.3) * mm});
            skPoint(sketch, "E43.visualSharp", {"position": v(83.5, -42.09) * mm});
            skArc(sketch, "E43.filletArc", {"start": v(81.7, -41.18) * mm, "mid": v(83.25, -41.28) * mm, "end": v(84.4, -40.25) * mm});
            skPoint(sketch, "E44.visualSharp", {"position": v(88.55, -30.06) * mm});
            skArc(sketch, "E44.filletArc", {"start": v(87.87, -31.98) * mm, "mid": v(87.8, -30.44) * mm, "end": v(86.63, -29.4) * mm});
            skPoint(sketch, "E45.visualSharp", {"position": v(66.36, -22.53) * mm});
            skArc(sketch, "E45.filletArc", {"start": v(68.23, -23.16) * mm, "mid": v(66.73, -23.25) * mm, "end": v(65.71, -24.36) * mm});
            skPoint(sketch, "E46.visualSharp", {"position": v(62.58, -31.54) * mm});
            skArc(sketch, "E46.filletArc", {"start": v(63.43, -29.8) * mm, "mid": v(63.35, -31.3) * mm, "end": v(64.34, -32.43) * mm});
            skPoint(sketch, "E47.visualSharp", {"position": v(61.73, -33.17) * mm});
            skArc(sketch, "E47.filletArc", {"start": v(63.47, -34.1) * mm, "mid": v(61.97, -33.94) * mm, "end": v(60.79, -34.87) * mm});
            skPoint(sketch, "E48.visualSharp", {"position": v(56.52, -41.44) * mm});
            skArc(sketch, "E48.filletArc", {"start": v(57.64, -39.85) * mm, "mid": v(57.32, -41.32) * mm, "end": v(58.1, -42.6) * mm});
            skPoint(sketch, "E49.visualSharp", {"position": v(55.41, -42.9) * mm});
            skArc(sketch, "E49.filletArc", {"start": v(56.97, -44.11) * mm, "mid": v(55.52, -43.7) * mm, "end": v(54.2, -44.42) * mm});
            skPoint(sketch, "E50.visualSharp", {"position": v(48.9, -50.2) * mm});
            skArc(sketch, "E50.filletArc", {"start": v(50.27, -48.82) * mm, "mid": v(49.7, -50.22) * mm, "end": v(50.28, -51.61) * mm});
            skPoint(sketch, "E51.visualSharp", {"position": v(66.93, -20.78) * mm});
            skArc(sketch, "E51.filletArc", {"start": v(67.48, -18.92) * mm, "mid": v(67.65, -20.41) * mm, "end": v(68.81, -21.37) * mm});
            skPoint(sketch, "E52.visualSharp", {"position": v(69.17, -11.26) * mm});
            skArc(sketch, "E52.filletArc", {"start": v(71.12, -11.58) * mm, "mid": v(69.65, -11.92) * mm, "end": v(68.83, -13.18) * mm});
            skPoint(sketch, "E53.visualSharp", {"position": v(92.3, -15.03) * mm});
            skArc(sketch, "E53.filletArc", {"start": v(91.94, -17.04) * mm, "mid": v(91.61, -15.53) * mm, "end": v(90.3, -14.7) * mm});
            skPoint(sketch, "E54.visualSharp", {"position": v(89.3, -27.73) * mm});
            skArc(sketch, "E54.filletArc", {"start": v(87.37, -27.13) * mm, "mid": v(88.92, -26.98) * mm, "end": v(89.89, -25.77) * mm});
            skPoint(sketch, "E55.visualSharp", {"position": v(92.66, -12.6) * mm});
            skArc(sketch, "E55.filletArc", {"start": v(90.65, -12.34) * mm, "mid": v(92.15, -11.93) * mm, "end": v(92.91, -10.58) * mm});
            skPoint(sketch, "E56.visualSharp", {"position": v(93.5, 0.4) * mm});
            skArc(sketch, "E56.filletArc", {"start": v(93.5, -1.63) * mm, "mid": v(92.92, -0.2) * mm, "end": v(91.49, 0.4) * mm});
            skPoint(sketch, "E57.visualSharp", {"position": v(70.08, 0.3) * mm});
            skArc(sketch, "E57.filletArc", {"start": v(72.05, 0.32) * mm, "mid": v(70.66, -0.26) * mm, "end": v(70.06, -1.64) * mm});
            skPoint(sketch, "E58.visualSharp", {"position": v(69.44, -9.45) * mm});
            skArc(sketch, "E58.filletArc", {"start": v(69.68, -7.52) * mm, "mid": v(70.09, -8.97) * mm, "end": v(71.4, -9.71) * mm});
            skPoint(sketch, "E59.visualSharp", {"position": v(93.47, 2.86) * mm});
            skArc(sketch, "E59.filletArc", {"start": v(91.45, 2.8) * mm, "mid": v(92.86, 3.44) * mm, "end": v(93.38, 4.9) * mm});
            skPoint(sketch, "E60.visualSharp", {"position": v(69.07, 11.87) * mm});
            skArc(sketch, "E60.filletArc", {"start": v(71.01, 12.2) * mm, "mid": v(69.73, 11.4) * mm, "end": v(69.37, 9.95) * mm});
            skPoint(sketch, "E61.visualSharp", {"position": v(70.05, 2.14) * mm});
            skArc(sketch, "E61.filletArc", {"start": v(69.96, 4.08) * mm, "mid": v(70.6, 2.73) * mm, "end": v(72.02, 2.2) * mm});
            skPoint(sketch, "E62.visualSharp", {"position": v(92.16, 15.84) * mm});
            skArc(sketch, "E62.filletArc", {"start": v(92.48, 13.82) * mm, "mid": v(91.68, 15.14) * mm, "end": v(90.17, 15.5) * mm});
            skPoint(sketch, "E63.visualSharp", {"position": v(-48.9, -50.2) * mm});
            skArc(sketch, "E63.filletArc", {"start": v(-50.28, -51.61) * mm, "mid": v(-49.7, -50.22) * mm, "end": v(-50.27, -48.82) * mm});
            skPoint(sketch, "E64.visualSharp", {"position": v(-55.41, -42.9) * mm});
            skArc(sketch, "E64.filletArc", {"start": v(-54.2, -44.43) * mm, "mid": v(-55.52, -43.7) * mm, "end": v(-56.97, -44.11) * mm});
            skPoint(sketch, "E65.visualSharp", {"position": v(-56.51, -41.44) * mm});
            skArc(sketch, "E65.filletArc", {"start": v(-58.1, -42.6) * mm, "mid": v(-57.32, -41.33) * mm, "end": v(-57.64, -39.86) * mm});
            skPoint(sketch, "E66.visualSharp", {"position": v(-61.73, -33.17) * mm});
            skArc(sketch, "E66.filletArc", {"start": v(-60.79, -34.87) * mm, "mid": v(-61.97, -33.94) * mm, "end": v(-63.47, -34.1) * mm});
            skPoint(sketch, "E67.visualSharp", {"position": v(-62.58, -31.54) * mm});
            skArc(sketch, "E67.filletArc", {"start": v(-64.34, -32.43) * mm, "mid": v(-63.35, -31.3) * mm, "end": v(-63.43, -29.8) * mm});
            skPoint(sketch, "E68.visualSharp", {"position": v(-66.36, -22.53) * mm});
            skArc(sketch, "E68.filletArc", {"start": v(-65.7, -24.36) * mm, "mid": v(-66.73, -23.25) * mm, "end": v(-68.23, -23.16) * mm});
            skPoint(sketch, "E69.visualSharp", {"position": v(-69.17, -11.27) * mm});
            skArc(sketch, "E69.filletArc", {"start": v(-68.83, -13.18) * mm, "mid": v(-69.65, -11.92) * mm, "end": v(-71.12, -11.58) * mm});
            skPoint(sketch, "E70.visualSharp", {"position": v(-66.93, -20.78) * mm});
            skArc(sketch, "E70.filletArc", {"start": v(-68.81, -21.37) * mm, "mid": v(-67.65, -20.41) * mm, "end": v(-67.48, -18.92) * mm});
            skPoint(sketch, "E71.visualSharp", {"position": v(-69.44, -9.45) * mm});
            skArc(sketch, "E71.filletArc", {"start": v(-71.4, -9.72) * mm, "mid": v(-70.09, -8.97) * mm, "end": v(-69.68, -7.52) * mm});
            skPoint(sketch, "E72.visualSharp", {"position": v(-70.08, 0.3) * mm});
            skArc(sketch, "E72.filletArc", {"start": v(-70.06, -1.64) * mm, "mid": v(-70.66, -0.26) * mm, "end": v(-72.05, 0.31) * mm});
            skPoint(sketch, "E73.visualSharp", {"position": v(-69.07, 11.87) * mm});
            skArc(sketch, "E73.filletArc", {"start": v(-69.37, 9.95) * mm, "mid": v(-69.73, 11.4) * mm, "end": v(-71.01, 12.2) * mm});
            skPoint(sketch, "E74.visualSharp", {"position": v(-70.05, 2.14) * mm});
            skArc(sketch, "E74.filletArc", {"start": v(-72.02, 2.2) * mm, "mid": v(-70.6, 2.72) * mm, "end": v(-69.96, 4.08) * mm});
            skPoint(sketch, "E75.visualSharp", {"position": v(-92.16, 15.84) * mm});
            skArc(sketch, "E75.filletArc", {"start": v(-90.17, 15.5) * mm, "mid": v(-91.68, 15.14) * mm, "end": v(-92.48, 13.82) * mm});
            skPoint(sketch, "E76.visualSharp", {"position": v(-93.47, 2.85) * mm});
            skArc(sketch, "E76.filletArc", {"start": v(-93.38, 4.9) * mm, "mid": v(-92.86, 3.44) * mm, "end": v(-91.45, 2.8) * mm});
            skPoint(sketch, "E77.visualSharp", {"position": v(-93.5, 0.4) * mm});
            skArc(sketch, "E77.filletArc", {"start": v(-91.49, 0.4) * mm, "mid": v(-92.92, -0.2) * mm, "end": v(-93.5, -1.64) * mm});
            skPoint(sketch, "E78.visualSharp", {"position": v(-92.66, -12.61) * mm});
            skArc(sketch, "E78.filletArc", {"start": v(-92.9, -10.58) * mm, "mid": v(-92.15, -11.94) * mm, "end": v(-90.65, -12.34) * mm});
            skPoint(sketch, "E79.visualSharp", {"position": v(-89.3, -27.73) * mm});
            skArc(sketch, "E79.filletArc", {"start": v(-89.89, -25.77) * mm, "mid": v(-88.92, -26.98) * mm, "end": v(-87.37, -27.13) * mm});
            skPoint(sketch, "E80.visualSharp", {"position": v(-88.55, -30.06) * mm});
            skArc(sketch, "E80.filletArc", {"start": v(-86.63, -29.4) * mm, "mid": v(-87.8, -30.44) * mm, "end": v(-87.87, -31.99) * mm});
            skPoint(sketch, "E81.visualSharp", {"position": v(-92.3, -15.03) * mm});
            skArc(sketch, "E81.filletArc", {"start": v(-90.3, -14.7) * mm, "mid": v(-91.61, -15.53) * mm, "end": v(-91.94, -17.05) * mm});
            skPoint(sketch, "E82.visualSharp", {"position": v(-83.5, -42.1) * mm});
            skArc(sketch, "E82.filletArc", {"start": v(-84.4, -40.26) * mm, "mid": v(-83.24, -41.29) * mm, "end": v(-81.7, -41.18) * mm});
            skPoint(sketch, "E83.visualSharp", {"position": v(-75.41, -55.3) * mm});
            skArc(sketch, "E83.filletArc", {"start": v(-76.6, -53.63) * mm, "mid": v(-75.29, -54.46) * mm, "end": v(-73.78, -54.1) * mm});
            skPoint(sketch, "E84.visualSharp", {"position": v(-82.37, -44.26) * mm});
            skArc(sketch, "E84.filletArc", {"start": v(-80.6, -43.3) * mm, "mid": v(-81.57, -44.51) * mm, "end": v(-81.38, -46.05) * mm});
            skPoint(sketch, "E85.visualSharp", {"position": v(-73.94, -57.25) * mm});
            skArc(sketch, "E85.filletArc", {"start": v(-72.34, -56.01) * mm, "mid": v(-73.1, -57.36) * mm, "end": v(-72.67, -58.85) * mm});
            skPoint(sketch, "E86.visualSharp", {"position": v(-65.25, -66.98) * mm});
            skArc(sketch, "E86.filletArc", {"start": v(-66.7, -65.54) * mm, "mid": v(-65.27, -66.14) * mm, "end": v(-63.84, -65.53) * mm});
            skPoint(sketch, "E87.visualSharp", {"position": v(-13.42, 92.54) * mm});
            skArc(sketch, "E87.filletArc", {"start": v(-13.13, 90.54) * mm, "mid": v(-13.93, 91.87) * mm, "end": v(-15.44, 92.23) * mm});
            skPoint(sketch, "E88.visualSharp", {"position": v(13.42, 92.54) * mm});
            skArc(sketch, "E88.filletArc", {"start": v(15.44, 92.23) * mm, "mid": v(13.93, 91.87) * mm, "end": v(13.13, 90.54) * mm});
            skPoint(sketch, "E89.visualSharp", {"position": v(-10.05, 69.35) * mm});
            skArc(sketch, "E89.filletArc", {"start": v(-11.98, 69.05) * mm, "mid": v(-10.7, 69.85) * mm, "end": v(-10.34, 71.3) * mm});
            skPoint(sketch, "E90.visualSharp", {"position": v(-83.87, 41.36) * mm});
            skArc(sketch, "E90.filletArc", {"start": v(-82.94, 43.18) * mm, "mid": v(-83.07, 41.63) * mm, "end": v(-82.05, 40.46) * mm});
            skPoint(sketch, "E91.visualSharp", {"position": v(-77.3, 52.63) * mm});
            skArc(sketch, "E91.filletArc", {"start": v(-75.62, 51.49) * mm, "mid": v(-77.14, 51.8) * mm, "end": v(-78.43, 50.92) * mm});
            skPoint(sketch, "E92.visualSharp", {"position": v(-75.9, 54.63) * mm});
            skArc(sketch, "E92.filletArc", {"start": v(-74.68, 56.28) * mm, "mid": v(-75.06, 54.77) * mm, "end": v(-74.25, 53.45) * mm});
            skPoint(sketch, "E93.visualSharp", {"position": v(-67.55, 64.66) * mm});
            skArc(sketch, "E93.filletArc", {"start": v(-66.09, 63.26) * mm, "mid": v(-67.54, 63.82) * mm, "end": v(-68.95, 63.17) * mm});
            skPoint(sketch, "E94.visualSharp", {"position": v(-65.83, 66.4) * mm});
            skArc(sketch, "E94.filletArc", {"start": v(-64.37, 67.83) * mm, "mid": v(-65, 66.41) * mm, "end": v(-64.41, 64.97) * mm});
            skPoint(sketch, "E95.visualSharp", {"position": v(-55.95, 74.92) * mm});
            skArc(sketch, "E95.filletArc", {"start": v(-54.74, 73.3) * mm, "mid": v(-56.08, 74.1) * mm, "end": v(-57.58, 73.68) * mm});
            skPoint(sketch, "E96.visualSharp", {"position": v(-53.97, 76.36) * mm});
            skArc(sketch, "E96.filletArc", {"start": v(-52.29, 77.52) * mm, "mid": v(-53.14, 76.23) * mm, "end": v(-52.8, 74.71) * mm});
            skPoint(sketch, "E97.visualSharp", {"position": v(-42.82, 83.13) * mm});
            skArc(sketch, "E97.filletArc", {"start": v(-41.9, 81.33) * mm, "mid": v(-43.08, 82.33) * mm, "end": v(-44.62, 82.18) * mm});
            skPoint(sketch, "E98.visualSharp", {"position": v(-40.63, 84.22) * mm});
            skArc(sketch, "E98.filletArc", {"start": v(-38.78, 85.1) * mm, "mid": v(-39.83, 83.95) * mm, "end": v(-39.75, 82.4) * mm});
            skPoint(sketch, "E99.visualSharp", {"position": v(-28.5, 89.06) * mm});
            skArc(sketch, "E99.filletArc", {"start": v(-27.9, 87.13) * mm, "mid": v(-28.9, 88.31) * mm, "end": v(-30.45, 88.41) * mm});
            skPoint(sketch, "E100.visualSharp", {"position": v(-26.17, 89.77) * mm});
            skArc(sketch, "E100.filletArc", {"start": v(-24.2, 90.32) * mm, "mid": v(-25.43, 89.37) * mm, "end": v(-25.6, 87.83) * mm});
            skPoint(sketch, "E101.visualSharp", {"position": v(-19.61, 67.28) * mm});
            skArc(sketch, "E101.filletArc", {"start": v(-20.16, 69.17) * mm, "mid": v(-19.23, 68) * mm, "end": v(-17.74, 67.8) * mm});
            skPoint(sketch, "E102.visualSharp", {"position": v(-62.85, 31) * mm});
            skArc(sketch, "E102.filletArc", {"start": v(-64.62, 31.87) * mm, "mid": v(-63.12, 31.76) * mm, "end": v(-61.97, 32.73) * mm});
            skPoint(sketch, "E103.visualSharp", {"position": v(-56.88, 40.94) * mm});
            skArc(sketch, "E103.filletArc", {"start": v(-58.48, 42.1) * mm, "mid": v(-57.01, 41.74) * mm, "end": v(-55.72, 42.5) * mm});
            skPoint(sketch, "E104.visualSharp", {"position": v(-50.62, 48.46) * mm});
            skArc(sketch, "E104.filletArc", {"start": v(-51.95, 47.04) * mm, "mid": v(-51.43, 48.45) * mm, "end": v(-52.05, 49.82) * mm});
            skPoint(sketch, "E105.visualSharp", {"position": v(-57.93, 39.44) * mm});
            skArc(sketch, "E105.filletArc", {"start": v(-59, 37.82) * mm, "mid": v(-58.72, 39.3) * mm, "end": v(-59.56, 40.55) * mm});
            skPoint(sketch, "E106.visualSharp", {"position": v(-49.34, 49.77) * mm});
            skArc(sketch, "E106.filletArc", {"start": v(-50.73, 51.17) * mm, "mid": v(-49.34, 50.58) * mm, "end": v(-47.94, 51.12) * mm});
            skPoint(sketch, "E107.visualSharp", {"position": v(-41.93, 56.15) * mm});
            skArc(sketch, "E107.filletArc", {"start": v(-43.47, 54.97) * mm, "mid": v(-42.73, 56.28) * mm, "end": v(-43.11, 57.73) * mm});
            skPoint(sketch, "E108.visualSharp", {"position": v(-40.45, 57.23) * mm});
            skArc(sketch, "E108.filletArc", {"start": v(-41.59, 58.84) * mm, "mid": v(-40.32, 58.03) * mm, "end": v(-38.84, 58.33) * mm});
            skPoint(sketch, "E109.visualSharp", {"position": v(-30.45, 63.12) * mm});
            skArc(sketch, "E109.filletArc", {"start": v(-31.3, 64.9) * mm, "mid": v(-30.19, 63.89) * mm, "end": v(-28.68, 63.94) * mm});
            skPoint(sketch, "E110.visualSharp", {"position": v(-21.37, 66.74) * mm});
            skArc(sketch, "E110.filletArc", {"start": v(-23.2, 66.12) * mm, "mid": v(-22.08, 67.12) * mm, "end": v(-21.97, 68.62) * mm});
            skPoint(sketch, "E111.visualSharp", {"position": v(10.05, 69.35) * mm});
            skArc(sketch, "E111.filletArc", {"start": v(10.34, 71.3) * mm, "mid": v(10.7, 69.85) * mm, "end": v(11.98, 69.05) * mm});
            skPoint(sketch, "E112.visualSharp", {"position": v(19.6, 67.28) * mm});
            skArc(sketch, "E112.filletArc", {"start": v(17.73, 67.8) * mm, "mid": v(19.23, 68) * mm, "end": v(20.16, 69.17) * mm});
            skPoint(sketch, "E113.visualSharp", {"position": v(30.44, 63.12) * mm});
            skArc(sketch, "E113.filletArc", {"start": v(28.68, 63.94) * mm, "mid": v(30.19, 63.89) * mm, "end": v(31.3, 64.9) * mm});
            skPoint(sketch, "E114.visualSharp", {"position": v(32.09, 62.3) * mm});
            skArc(sketch, "E114.filletArc", {"start": v(32.99, 64.06) * mm, "mid": v(32.85, 62.56) * mm, "end": v(33.8, 61.39) * mm});
            skPoint(sketch, "E115.visualSharp", {"position": v(41.93, 56.15) * mm});
            skArc(sketch, "E115.filletArc", {"start": v(43.1, 57.73) * mm, "mid": v(42.73, 56.28) * mm, "end": v(43.47, 54.97) * mm});
            skPoint(sketch, "E116.visualSharp", {"position": v(50.62, 48.46) * mm});
            skArc(sketch, "E116.filletArc", {"start": v(52.05, 49.83) * mm, "mid": v(51.43, 48.45) * mm, "end": v(51.95, 47.04) * mm});
            skPoint(sketch, "E117.visualSharp", {"position": v(56.87, 40.95) * mm});
            skArc(sketch, "E117.filletArc", {"start": v(55.72, 42.5) * mm, "mid": v(57.01, 41.74) * mm, "end": v(58.47, 42.1) * mm});
            skPoint(sketch, "E118.visualSharp", {"position": v(57.93, 39.44) * mm});
            skArc(sketch, "E118.filletArc", {"start": v(59.56, 40.55) * mm, "mid": v(58.72, 39.3) * mm, "end": v(59, 37.82) * mm});
            skPoint(sketch, "E119.visualSharp", {"position": v(62.85, 31) * mm});
            skArc(sketch, "E119.filletArc", {"start": v(61.97, 32.73) * mm, "mid": v(63.12, 31.76) * mm, "end": v(64.62, 31.87) * mm});
            skPoint(sketch, "E120.visualSharp", {"position": v(49.34, 49.77) * mm});
            skArc(sketch, "E120.filletArc", {"start": v(47.94, 51.12) * mm, "mid": v(49.34, 50.58) * mm, "end": v(50.72, 51.17) * mm});
            skPoint(sketch, "E121.visualSharp", {"position": v(83.87, 41.36) * mm});
            skArc(sketch, "E121.filletArc", {"start": v(82.05, 40.46) * mm, "mid": v(83.07, 41.63) * mm, "end": v(82.94, 43.18) * mm});
            skPoint(sketch, "E122.visualSharp", {"position": v(75.89, 54.64) * mm});
            skArc(sketch, "E122.filletArc", {"start": v(74.25, 53.45) * mm, "mid": v(75.06, 54.78) * mm, "end": v(74.68, 56.28) * mm});
            skPoint(sketch, "E123.visualSharp", {"position": v(65.83, 66.41) * mm});
            skArc(sketch, "E123.filletArc", {"start": v(64.4, 64.98) * mm, "mid": v(64.99, 66.41) * mm, "end": v(64.36, 67.83) * mm});
            skPoint(sketch, "E124.visualSharp", {"position": v(55.95, 74.93) * mm});
            skArc(sketch, "E124.filletArc", {"start": v(57.57, 73.69) * mm, "mid": v(56.08, 74.1) * mm, "end": v(54.74, 73.3) * mm});
            skPoint(sketch, "E125.visualSharp", {"position": v(42.81, 83.13) * mm});
            skArc(sketch, "E125.filletArc", {"start": v(44.62, 82.18) * mm, "mid": v(43.08, 82.33) * mm, "end": v(41.89, 81.34) * mm});
            skPoint(sketch, "E126.visualSharp", {"position": v(53.97, 76.37) * mm});
            skArc(sketch, "E126.filletArc", {"start": v(52.8, 74.71) * mm, "mid": v(53.13, 76.23) * mm, "end": v(52.29, 77.53) * mm});
            skPoint(sketch, "E127.visualSharp", {"position": v(26.17, 89.78) * mm});
            skArc(sketch, "E127.filletArc", {"start": v(25.6, 87.83) * mm, "mid": v(25.42, 89.38) * mm, "end": v(24.2, 90.33) * mm});
            skPoint(sketch, "E128.visualSharp", {"position": v(28.5, 89.06) * mm});
            skArc(sketch, "E128.filletArc", {"start": v(30.45, 88.42) * mm, "mid": v(28.9, 88.31) * mm, "end": v(27.89, 87.13) * mm});
            skPoint(sketch, "E129.visualSharp", {"position": v(40.62, 84.23) * mm});
            skArc(sketch, "E129.filletArc", {"start": v(39.75, 82.4) * mm, "mid": v(39.82, 83.95) * mm, "end": v(38.77, 85.1) * mm});
            skPoint(sketch, "E130.visualSharp", {"position": v(67.55, 64.67) * mm});
            skArc(sketch, "E130.filletArc", {"start": v(68.94, 63.17) * mm, "mid": v(67.54, 63.82) * mm, "end": v(66.09, 63.27) * mm});
            skPoint(sketch, "E131.visualSharp", {"position": v(77.3, 52.63) * mm});
            skArc(sketch, "E131.filletArc", {"start": v(78.43, 50.93) * mm, "mid": v(77.14, 51.8) * mm, "end": v(75.62, 51.5) * mm});
            skPoint(sketch, "E132.visualSharp", {"position": v(-32.09, 62.3) * mm});
            skArc(sketch, "E132.filletArc", {"start": v(-33.8, 61.39) * mm, "mid": v(-32.86, 62.56) * mm, "end": v(-33, 64.06) * mm});
            skPoint(sketch, "E133.visualSharp", {"position": v(21.36, 66.74) * mm});
            skArc(sketch, "E133.filletArc", {"start": v(21.96, 68.62) * mm, "mid": v(22.08, 67.12) * mm, "end": v(23.2, 66.13) * mm});
            skPoint(sketch, "E134.visualSharp", {"position": v(40.45, 57.23) * mm});
            skArc(sketch, "E134.filletArc", {"start": v(38.84, 58.33) * mm, "mid": v(40.32, 58.03) * mm, "end": v(41.58, 58.84) * mm});
            skSolve(sketch);
        }
        {
            var Q0;
            Q0=makeQuery(id+"F3.imprint","IMPRINT",FACE,{"disambiguationData":[TD([[makeQuery(id+"F3.imprint","IMPRINT",EDGE,{"derivedFrom":sQuery(id+"F3.wireOp",EDGE,"E38.3.0")}),1.0]])]});
            var Q1;
            Q1=makeQuery(id+"F3.imprint","IMPRINT",FACE,{"disambiguationData":[TD([[makeQuery(id+"F3.imprint","IMPRINT",EDGE,{"derivedFrom":sQuery(id+"F3.wireOp",EDGE,"E38.3.2")}),-1.0]])]});
            var Q2;
            Q2=makeQuery(id+"F3.imprint","IMPRINT",FACE,{"disambiguationData":[TD([[makeQuery(id+"F3.imprint","IMPRINT",EDGE,{"derivedFrom":sQuery(id+"F3.wireOp",EDGE,"E38.3.4")}),1.0]])]});
            var Q3;
            Q3=makeQuery(id+"F3.imprint","IMPRINT",FACE,{"disambiguationData":[TD([[makeQuery(id+"F3.imprint","IMPRINT",EDGE,{"derivedFrom":sQuery(id+"F3.wireOp",EDGE,"E38.2.0")}),1.0]])]});
            var Q4;
            Q4=makeQuery(id+"F3.imprint","IMPRINT",FACE,{"disambiguationData":[TD([[makeQuery(id+"F3.imprint","IMPRINT",EDGE,{"derivedFrom":sQuery(id+"F3.wireOp",EDGE,"E38.2.2")}),-1.0]])]});
            var Q5;
            Q5=makeQuery(id+"F3.imprint","IMPRINT",FACE,{"disambiguationData":[TD([[makeQuery(id+"F3.imprint","IMPRINT",EDGE,{"derivedFrom":sQuery(id+"F3.wireOp",EDGE,"E38.2.4")}),1.0]])]});
            var Q6;
            Q6=makeQuery(id+"F3.imprint","IMPRINT",FACE,{"disambiguationData":[TD([[makeQuery(id+"F3.imprint","IMPRINT",EDGE,{"derivedFrom":sQuery(id+"F3.wireOp",EDGE,"E38.1.0")}),1.0]])]});
            var Q7;
            Q7=makeQuery(id+"F3.imprint","IMPRINT",FACE,{"disambiguationData":[TD([[makeQuery(id+"F3.imprint","IMPRINT",EDGE,{"derivedFrom":sQuery(id+"F3.wireOp",EDGE,"E38.1.2")}),-1.0]])]});
            var Q8;
            Q8=makeQuery(id+"F3.imprint","IMPRINT",FACE,{"disambiguationData":[TD([[makeQuery(id+"F3.imprint","IMPRINT",EDGE,{"derivedFrom":sQuery(id+"F3.wireOp",EDGE,"E38.1.4")}),1.0]])]});
            var Q9;
            Q9=makeQuery(id+"F3.imprint","IMPRINT",FACE,{"disambiguationData":[TD([[makeQuery(id+"F3.imprint","IMPRINT",EDGE,{"derivedFrom":sQuery(id+"F3.wireOp",EDGE,"E14")}),-1.0]])]});
            var Q10;
            Q10=makeQuery(id+"F3.imprint","IMPRINT",FACE,{"disambiguationData":[TD([[makeQuery(id+"F3.imprint","IMPRINT",EDGE,{"derivedFrom":sQuery(id+"F3.wireOp",EDGE,"E19")}),-1.0]])]});
            var Q11;
            Q11=makeQuery(id+"F3.imprint","IMPRINT",FACE,{"disambiguationData":[TD([[makeQuery(id+"F3.imprint","IMPRINT",EDGE,{"derivedFrom":sQuery(id+"F3.wireOp",EDGE,"E27")}),-1.0]])]});
            extrude(context, id + "F4", {"entities" : qUnion([Q0, Q1, Q2, Q3, Q4, Q5, Q6, Q7, Q8, Q9, Q10, Q11]), "operationType" : NewBodyOperationType.REMOVE, "oppositeDirection" : true, "depth" : 4.5 * mm});
        }
        {
            var Q0;
            Q0=makeQuery(id+"F3.imprint","IMPRINT",FACE,{"disambiguationData":[TD([[makeQuery(id+"F3.imprint","IMPRINT",EDGE,{"derivedFrom":sQuery(id+"F3.wireOp",EDGE,"E38.3.1")}),1.0]])]});
            var Q1;
            Q1=makeQuery(id+"F3.imprint","IMPRINT",FACE,{"disambiguationData":[TD([[makeQuery(id+"F3.imprint","IMPRINT",EDGE,{"derivedFrom":sQuery(id+"F3.wireOp",EDGE,"E38.3.3")}),1.0]])]});
            var Q2;
            Q2=makeQuery(id+"F3.imprint","IMPRINT",FACE,{"disambiguationData":[TD([[makeQuery(id+"F3.imprint","IMPRINT",EDGE,{"derivedFrom":sQuery(id+"F3.wireOp",EDGE,"E38.3.10")}),1.0]])]});
            var Q3;
            Q3=makeQuery(id+"F3.imprint","IMPRINT",FACE,{"disambiguationData":[TD([[makeQuery(id+"F3.imprint","IMPRINT",EDGE,{"derivedFrom":sQuery(id+"F3.wireOp",EDGE,"E38.2.1")}),1.0]])]});
            var Q4;
            Q4=makeQuery(id+"F3.imprint","IMPRINT",FACE,{"disambiguationData":[TD([[makeQuery(id+"F3.imprint","IMPRINT",EDGE,{"derivedFrom":sQuery(id+"F3.wireOp",EDGE,"E38.2.3")}),1.0]])]});
            var Q5;
            Q5=makeQuery(id+"F3.imprint","IMPRINT",FACE,{"disambiguationData":[TD([[makeQuery(id+"F3.imprint","IMPRINT",EDGE,{"derivedFrom":sQuery(id+"F3.wireOp",EDGE,"E38.2.10")}),1.0]])]});
            var Q6;
            Q6=makeQuery(id+"F3.imprint","IMPRINT",FACE,{"disambiguationData":[TD([[makeQuery(id+"F3.imprint","IMPRINT",EDGE,{"derivedFrom":sQuery(id+"F3.wireOp",EDGE,"E38.1.1")}),1.0]])]});
            var Q7;
            Q7=makeQuery(id+"F3.imprint","IMPRINT",FACE,{"disambiguationData":[TD([[makeQuery(id+"F3.imprint","IMPRINT",EDGE,{"derivedFrom":sQuery(id+"F3.wireOp",EDGE,"E38.1.3")}),1.0]])]});
            var Q8;
            Q8=makeQuery(id+"F3.imprint","IMPRINT",FACE,{"disambiguationData":[TD([[makeQuery(id+"F3.imprint","IMPRINT",EDGE,{"derivedFrom":sQuery(id+"F3.wireOp",EDGE,"E38.1.10")}),1.0]])]});
            var Q9;
            Q9=makeQuery(id+"F3.imprint","IMPRINT",FACE,{"disambiguationData":[TD([[makeQuery(id+"F3.imprint","IMPRINT",EDGE,{"derivedFrom":sQuery(id+"F3.wireOp",EDGE,"E21")}),-1.0]])]});
            var Q10;
            Q10=makeQuery(id+"F3.imprint","IMPRINT",FACE,{"disambiguationData":[TD([[makeQuery(id+"F3.imprint","IMPRINT",EDGE,{"derivedFrom":sQuery(id+"F3.wireOp",EDGE,"E31")}),-1.0]])]});
            var Q11;
            Q11=makeQuery(id+"F3.imprint","IMPRINT",FACE,{"disambiguationData":[TD([[makeQuery(id+"F3.imprint","IMPRINT",EDGE,{"derivedFrom":sQuery(id+"F3.wireOp",EDGE,"E15")}),1.0]])]});
            extrude(context, id + "F5", {"entities" : qUnion([Q0, Q1, Q2, Q3, Q4, Q5, Q6, Q7, Q8, Q9, Q10, Q11]), "operationType" : NewBodyOperationType.REMOVE, "oppositeDirection" : true, "depth" : 2.5 * mm});
        }
    });
